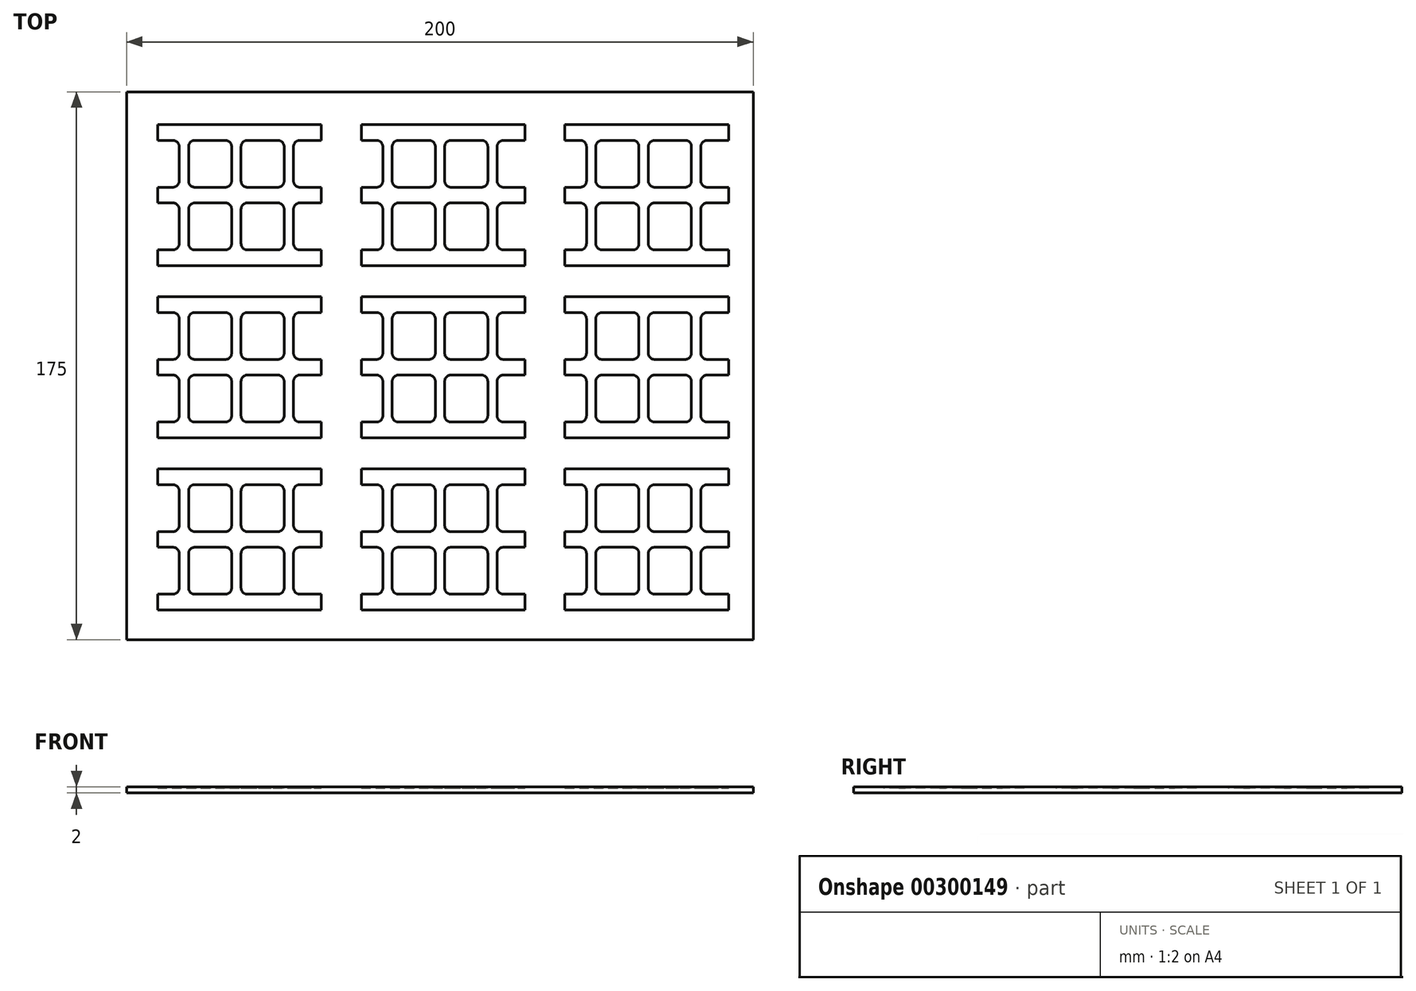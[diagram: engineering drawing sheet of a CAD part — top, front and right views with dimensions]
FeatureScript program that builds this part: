
annotation { "Feature Type Name" : "Feature", "Feature Type Description" : "" }
export const myFeature = defineFeature(function(context is Context, id is Id, definition is map)
    precondition{}
    {
        {
            var Q0;
            Q0=qCreatedBy(makeId("Top.planeOp"),FACE);
            var sketch = newSketch(context, id + "F0", { "sketchPlane" : qUnion([Q0])});
            skLineSegment(sketch, "E0.bottom", {"start": v(-3.5, 2.5) * mm, "end": v(-13.25, 2.5) * mm});
            skLineSegment(sketch, "E0.top", {"start": v(-3.5, 17.5) * mm, "end": v(-13.25, 17.5) * mm});
            skLineSegment(sketch, "E0.left", {"start": v(-1.5, 4.5) * mm, "end": v(-1.5, 15.5) * mm});
            skLineSegment(sketch, "E0.right", {"start": v(-15.25, 4.5) * mm, "end": v(-15.25, 15.5) * mm});
            skPoint(sketch, "E1.visualSharp", {"position": v(-15.25, 17.5) * mm});
            skArc(sketch, "E1.filletArc", {"start": v(-13.25, 17.5) * mm, "mid": v(-14.66, 16.91) * mm, "end": v(-15.25, 15.5) * mm});
            skPoint(sketch, "E2.visualSharp", {"position": v(-1.5, 17.5) * mm});
            skArc(sketch, "E2.filletArc", {"start": v(-1.5, 15.5) * mm, "mid": v(-2.09, 16.91) * mm, "end": v(-3.5, 17.5) * mm});
            skPoint(sketch, "E3.visualSharp", {"position": v(-1.5, 2.5) * mm});
            skArc(sketch, "E3.filletArc", {"start": v(-3.5, 2.5) * mm, "mid": v(-2.09, 3.09) * mm, "end": v(-1.5, 4.5) * mm});
            skPoint(sketch, "E4.visualSharp", {"position": v(-15.25, 2.5) * mm});
            skArc(sketch, "E4.filletArc", {"start": v(-15.25, 4.5) * mm, "mid": v(-14.66, 3.09) * mm, "end": v(-13.25, 2.5) * mm});
            skArc(sketch, "E5.MirrorCS", {"start": v(15.25, 4.5) * mm, "mid": v(14.66, 3.09) * mm, "end": v(13.25, 2.5) * mm});
            skArc(sketch, "E6.MirrorCS", {"start": v(13.25, 17.5) * mm, "mid": v(14.66, 16.91) * mm, "end": v(15.25, 15.5) * mm});
            skArc(sketch, "E7.MirrorCS", {"start": v(3.5, 2.5) * mm, "mid": v(2.09, 3.09) * mm, "end": v(1.5, 4.5) * mm});
            skArc(sketch, "E8.MirrorCS", {"start": v(1.5, 15.5) * mm, "mid": v(2.09, 16.91) * mm, "end": v(3.5, 17.5) * mm});
            skLineSegment(sketch, "E9.MirrorCS", {"start": v(3.5, 17.5) * mm, "end": v(13.25, 17.5) * mm});
            skLineSegment(sketch, "E10.MirrorCS", {"start": v(1.5, 4.5) * mm, "end": v(1.5, 15.5) * mm});
            skPoint(sketch, "E11.MirrorP", {"position": v(1.5, 17.5) * mm});
            skPoint(sketch, "E12.MirrorP", {"position": v(15.25, 2.5) * mm});
            skPoint(sketch, "E13.MirrorP", {"position": v(15.25, 17.5) * mm});
            skPoint(sketch, "E14.MirrorP", {"position": v(1.5, 2.5) * mm});
            skLineSegment(sketch, "E15.MirrorCS", {"start": v(3.5, 2.5) * mm, "end": v(13.25, 2.5) * mm});
            skLineSegment(sketch, "E16.MirrorCS", {"start": v(15.25, 4.5) * mm, "end": v(15.25, 15.5) * mm});
            skArc(sketch, "E17.MirrorCS", {"start": v(-1.5, -15.5) * mm, "mid": v(-2.09, -16.91) * mm, "end": v(-3.5, -17.5) * mm});
            skArc(sketch, "E18.MirrorCS", {"start": v(-3.5, -2.5) * mm, "mid": v(-2.09, -3.09) * mm, "end": v(-1.5, -4.5) * mm});
            skArc(sketch, "E19.MirrorCS", {"start": v(-13.25, -17.5) * mm, "mid": v(-14.66, -16.91) * mm, "end": v(-15.25, -15.5) * mm});
            skArc(sketch, "E20.MirrorCS", {"start": v(15.25, -4.5) * mm, "mid": v(14.66, -3.09) * mm, "end": v(13.25, -2.5) * mm});
            skArc(sketch, "E21.MirrorCS", {"start": v(-15.25, -4.5) * mm, "mid": v(-14.66, -3.09) * mm, "end": v(-13.25, -2.5) * mm});
            skArc(sketch, "E22.MirrorCS", {"start": v(13.25, -17.5) * mm, "mid": v(14.66, -16.91) * mm, "end": v(15.25, -15.5) * mm});
            skArc(sketch, "E23.MirrorCS", {"start": v(3.5, -2.5) * mm, "mid": v(2.09, -3.09) * mm, "end": v(1.5, -4.5) * mm});
            skArc(sketch, "E24.MirrorCS", {"start": v(1.5, -15.5) * mm, "mid": v(2.09, -16.91) * mm, "end": v(3.5, -17.5) * mm});
            skPoint(sketch, "E25.MirrorP", {"position": v(-15.25, -2.5) * mm});
            skLineSegment(sketch, "E26.MirrorCS", {"start": v(-1.5, -4.5) * mm, "end": v(-1.5, -15.5) * mm});
            skLineSegment(sketch, "E27.MirrorCS", {"start": v(15.25, -4.5) * mm, "end": v(15.25, -15.5) * mm});
            skPoint(sketch, "E28.MirrorP", {"position": v(-15.25, -17.5) * mm});
            skLineSegment(sketch, "E29.MirrorCS", {"start": v(3.5, -17.5) * mm, "end": v(13.25, -17.5) * mm});
            skLineSegment(sketch, "E30.MirrorCS", {"start": v(-15.25, -4.5) * mm, "end": v(-15.25, -15.5) * mm});
            skLineSegment(sketch, "E31.MirrorCS", {"start": v(-3.5, -17.5) * mm, "end": v(-13.25, -17.5) * mm});
            skPoint(sketch, "E32.MirrorP", {"position": v(-1.5, -17.5) * mm});
            skLineSegment(sketch, "E33.MirrorCS", {"start": v(1.5, -4.5) * mm, "end": v(1.5, -15.5) * mm});
            skLineSegment(sketch, "E34.MirrorCS", {"start": v(-3.5, -2.5) * mm, "end": v(-13.25, -2.5) * mm});
            skPoint(sketch, "E35.MirrorP", {"position": v(1.5, -17.5) * mm});
            skPoint(sketch, "E36.MirrorP", {"position": v(-1.5, -2.5) * mm});
            skPoint(sketch, "E37.MirrorP", {"position": v(15.25, -2.5) * mm});
            skPoint(sketch, "E38.MirrorP", {"position": v(15.25, -17.5) * mm});
            skPoint(sketch, "E39.MirrorP", {"position": v(1.5, -2.5) * mm});
            skLineSegment(sketch, "E40.MirrorCS", {"start": v(3.5, -2.5) * mm, "end": v(13.25, -2.5) * mm});
            skLineSegment(sketch, "E41", {"start": v(16.75, 36.36) * mm, "end": v(16.75, -33.16) * mm, "construction": true});
            skArc(sketch, "E42.MirrorCS", {"start": v(18.25, 4.5) * mm, "mid": v(18.84, 3.09) * mm, "end": v(20.25, 2.5) * mm});
            skArc(sketch, "E43.MirrorCS", {"start": v(20.25, -17.5) * mm, "mid": v(18.84, -16.91) * mm, "end": v(18.25, -15.5) * mm});
            skArc(sketch, "E44.MirrorCS", {"start": v(20.25, 17.5) * mm, "mid": v(18.84, 16.91) * mm, "end": v(18.25, 15.5) * mm});
            skArc(sketch, "E45.MirrorCS", {"start": v(18.25, -4.5) * mm, "mid": v(18.84, -3.09) * mm, "end": v(20.25, -2.5) * mm});
            skLineSegment(sketch, "E46.MirrorCS", {"start": v(25.12, -2.5) * mm, "end": v(20.25, -2.5) * mm});
            skLineSegment(sketch, "E47.MirrorCS", {"start": v(18.25, -4.5) * mm, "end": v(18.25, -15.5) * mm});
            skPoint(sketch, "E48.MirrorP", {"position": v(18.25, 2.5) * mm});
            skPoint(sketch, "E49.MirrorP", {"position": v(18.25, -2.5) * mm});
            skLineSegment(sketch, "E50.MirrorCS", {"start": v(25.12, 17.5) * mm, "end": v(20.25, 17.5) * mm});
            skPoint(sketch, "E51.MirrorP", {"position": v(18.25, -17.5) * mm});
            skLineSegment(sketch, "E52.MirrorCS", {"start": v(25.12, -17.5) * mm, "end": v(20.25, -17.5) * mm});
            skLineSegment(sketch, "E53.MirrorCS", {"start": v(18.25, 4.5) * mm, "end": v(18.25, 15.5) * mm});
            skPoint(sketch, "E54.MirrorP", {"position": v(18.25, 17.5) * mm});
            skLineSegment(sketch, "E55.MirrorCS", {"start": v(25.12, 2.5) * mm, "end": v(20.25, 2.5) * mm});
            skLineSegment(sketch, "E56.bottom", {"start": v(25.12, 22.5) * mm, "end": v(-25.12, 22.5) * mm});
            skLineSegment(sketch, "E56.top", {"start": v(25.12, -22.5) * mm, "end": v(-25.12, -22.5) * mm});
            skLineSegment(sketch, "E56.left", {"start": v(25.12, 22.5) * mm, "end": v(25.12, 17.5) * mm});
            skLineSegment(sketch, "E56.right", {"start": v(-25.12, 22.5) * mm, "end": v(-25.12, 17.5) * mm});
            skPoint(sketch, "E56.middle", {"position": v(0, 0) * mm});
            skArc(sketch, "E57.MirrorCS", {"start": v(-18.25, 4.5) * mm, "mid": v(-18.84, 3.09) * mm, "end": v(-20.25, 2.5) * mm});
            skArc(sketch, "E58.MirrorCS", {"start": v(-18.25, -4.5) * mm, "mid": v(-18.84, -3.09) * mm, "end": v(-20.25, -2.5) * mm});
            skArc(sketch, "E59.MirrorCS", {"start": v(-20.25, 17.5) * mm, "mid": v(-18.84, 16.91) * mm, "end": v(-18.25, 15.5) * mm});
            skArc(sketch, "E60.MirrorCS", {"start": v(-20.25, -17.5) * mm, "mid": v(-18.84, -16.91) * mm, "end": v(-18.25, -15.5) * mm});
            skPoint(sketch, "E61.MirrorP", {"position": v(-18.25, -2.5) * mm});
            skLineSegment(sketch, "E62.MirrorCS", {"start": v(-18.25, -4.5) * mm, "end": v(-18.25, -15.5) * mm});
            skPoint(sketch, "E63.MirrorP", {"position": v(-32, -17.5) * mm});
            skLineSegment(sketch, "E64.MirrorCS", {"start": v(-25.12, -2.5) * mm, "end": v(-20.25, -2.5) * mm});
            skPoint(sketch, "E65.MirrorP", {"position": v(-18.25, 2.5) * mm});
            skPoint(sketch, "E66.MirrorP", {"position": v(-18.25, 17.5) * mm});
            skPoint(sketch, "E67.MirrorP", {"position": v(-32, 17.5) * mm});
            skPoint(sketch, "E68.MirrorP", {"position": v(-18.25, -17.5) * mm});
            skLineSegment(sketch, "E69.MirrorCS", {"start": v(-25.12, 2.5) * mm, "end": v(-20.25, 2.5) * mm});
            skPoint(sketch, "E70.MirrorP", {"position": v(-32, 2.5) * mm});
            skPoint(sketch, "E71.MirrorP", {"position": v(-32, -2.5) * mm});
            skLineSegment(sketch, "E72.MirrorCS", {"start": v(-25.12, -17.5) * mm, "end": v(-20.25, -17.5) * mm});
            skLineSegment(sketch, "E73.MirrorCS", {"start": v(-25.12, 17.5) * mm, "end": v(-20.25, 17.5) * mm});
            skLineSegment(sketch, "E74.MirrorCS", {"start": v(-18.25, 4.5) * mm, "end": v(-18.25, 15.5) * mm});
            skLineSegment(sketch, "E75.trimOffspring", {"start": v(25.12, 2.5) * mm, "end": v(25.12, -2.5) * mm});
            skLineSegment(sketch, "E76.trimOffspring", {"start": v(25.12, -17.5) * mm, "end": v(25.12, -22.5) * mm});
            skPoint(sketch, "E77.MirrorCS.start.orphan", {"position": v(30, -2.5) * mm});
            skPoint(sketch, "E78.orphan", {"position": v(30, -17.5) * mm});
            skPoint(sketch, "E79.MirrorCS.start.orphan", {"position": v(30, 2.5) * mm});
            skPoint(sketch, "E80.MirrorCS.end.orphan", {"position": v(30, 17.5) * mm});
            skPoint(sketch, "E81.MirrorCS.start.orphan", {"position": v(-32, 15.5) * mm});
            skPoint(sketch, "E82.orphan", {"position": v(-30, 17.5) * mm});
            skLineSegment(sketch, "E83.trimOffspring", {"start": v(-25.12, 2.5) * mm, "end": v(-25.12, -2.5) * mm});
            skPoint(sketch, "E84.MirrorCS.end.orphan", {"position": v(-32, 4.5) * mm});
            skPoint(sketch, "E84.MirrorCS.start.orphan", {"position": v(-30, 2.5) * mm});
            skPoint(sketch, "E85.orphan", {"position": v(-30, -2.5) * mm});
            skPoint(sketch, "E86.MirrorCS.start.orphan", {"position": v(-32, -4.5) * mm});
            skPoint(sketch, "E87.MirrorCS.start.orphan", {"position": v(-32, -15.5) * mm});
            skPoint(sketch, "E88.orphan", {"position": v(-30, -17.5) * mm});
            skLineSegment(sketch, "E89.trimOffspring", {"start": v(-25.12, -17.5) * mm, "end": v(-25.12, -22.5) * mm});
            skLineSegment(sketch, "E90.direction1", {"start": v(-30, -17.5) * mm, "end": v(40, -17.5) * mm, "construction": true});
            skLineSegment(sketch, "E91.bottom", {"start": v(25.12, 22.5) * mm, "end": v(27.12, 22.5) * mm});
            skLineSegment(sketch, "E91.top", {"start": v(25.12, 17.5) * mm, "end": v(27.12, 17.5) * mm});
            skLineSegment(sketch, "E91.right", {"start": v(27.12, 22.5) * mm, "end": v(27.12, 17.5) * mm});
            skLineSegment(sketch, "E92.bottom", {"start": v(25.12, 2.5) * mm, "end": v(27.12, 2.5) * mm});
            skLineSegment(sketch, "E92.top", {"start": v(25.12, -2.5) * mm, "end": v(27.12, -2.5) * mm});
            skLineSegment(sketch, "E92.right", {"start": v(27.12, 2.5) * mm, "end": v(27.12, -2.5) * mm});
            skLineSegment(sketch, "E93.bottom", {"start": v(25.12, -17.5) * mm, "end": v(27.12, -17.5) * mm});
            skLineSegment(sketch, "E93.top", {"start": v(25.12, -22.5) * mm, "end": v(27.12, -22.5) * mm});
            skLineSegment(sketch, "E93.right", {"start": v(27.12, -17.5) * mm, "end": v(27.12, -22.5) * mm});
            skPoint(sketch, "E94.0.1.0", {"position": v(-15.25, 37.5) * mm});
            skPoint(sketch, "E94.0.1.1", {"position": v(-32, 70.5) * mm});
            skLineSegment(sketch, "E94.0.1.2", {"start": v(25.12, 57.5) * mm, "end": v(20.25, 57.5) * mm});
            skLineSegment(sketch, "E94.0.1.3", {"start": v(-18.25, 50.5) * mm, "end": v(-18.25, 39.5) * mm});
            skPoint(sketch, "E94.0.1.4", {"position": v(-15.25, 72.5) * mm});
            skPoint(sketch, "E94.0.1.5", {"position": v(-30, 37.5) * mm});
            skPoint(sketch, "E94.0.1.6", {"position": v(-18.25, 72.5) * mm});
            skPoint(sketch, "E94.0.1.7", {"position": v(-1.5, 37.5) * mm});
            skPoint(sketch, "E94.0.1.8", {"position": v(-32, 57.5) * mm});
            skPoint(sketch, "E94.0.1.9", {"position": v(-30, 72.5) * mm});
            skLineSegment(sketch, "E94.0.1.10", {"start": v(25.12, 77.5) * mm, "end": v(-25.12, 77.5) * mm});
            skLineSegment(sketch, "E94.0.1.11", {"start": v(-15.25, 50.5) * mm, "end": v(-15.25, 39.5) * mm});
            skLineSegment(sketch, "E94.0.1.12", {"start": v(25.12, 37.5) * mm, "end": v(25.12, 32.5) * mm});
            skLineSegment(sketch, "E94.0.1.13", {"start": v(27.12, 77.5) * mm, "end": v(27.12, 72.5) * mm});
            skLineSegment(sketch, "E94.0.1.14", {"start": v(25.12, 77.5) * mm, "end": v(25.12, 72.5) * mm});
            skLineSegment(sketch, "E94.0.1.15", {"start": v(-25.12, 52.5) * mm, "end": v(-20.25, 52.5) * mm});
            skLineSegment(sketch, "E94.0.1.16", {"start": v(1.5, 50.5) * mm, "end": v(1.5, 39.5) * mm});
            skPoint(sketch, "E94.0.1.17", {"position": v(-32, 72.5) * mm});
            skPoint(sketch, "E94.0.1.18", {"position": v(18.25, 57.5) * mm});
            skPoint(sketch, "E94.0.1.19", {"position": v(1.5, 37.5) * mm});
            skPoint(sketch, "E94.0.1.20", {"position": v(-1.5, 57.5) * mm});
            skPoint(sketch, "E94.0.1.21", {"position": v(-32, 52.5) * mm});
            skPoint(sketch, "E94.0.1.22", {"position": v(-32, 59.5) * mm});
            skLineSegment(sketch, "E94.0.1.23", {"start": v(25.12, 32.5) * mm, "end": v(-25.12, 32.5) * mm});
            skLineSegment(sketch, "E94.0.1.24", {"start": v(27.12, 37.5) * mm, "end": v(27.12, 32.5) * mm});
            skLineSegment(sketch, "E94.0.1.25", {"start": v(-25.12, 57.5) * mm, "end": v(-25.12, 52.5) * mm});
            skLineSegment(sketch, "E94.0.1.26", {"start": v(-25.12, 77.5) * mm, "end": v(-25.12, 72.5) * mm});
            skLineSegment(sketch, "E94.0.1.27", {"start": v(25.12, 52.5) * mm, "end": v(20.25, 52.5) * mm});
            skLineSegment(sketch, "E94.0.1.28", {"start": v(-3.5, 52.5) * mm, "end": v(-13.25, 52.5) * mm});
            skPoint(sketch, "E94.0.1.29", {"position": v(-1.5, 72.5) * mm});
            skPoint(sketch, "E94.0.1.30", {"position": v(-18.25, 37.5) * mm});
            skPoint(sketch, "E94.0.1.31", {"position": v(18.25, 52.5) * mm});
            skPoint(sketch, "E94.0.1.32", {"position": v(-1.5, 52.5) * mm});
            skPoint(sketch, "E94.0.1.33", {"position": v(1.5, 72.5) * mm});
            skPoint(sketch, "E94.0.1.34", {"position": v(30, 52.5) * mm});
            skPoint(sketch, "E94.0.1.35", {"position": v(-30, 57.5) * mm});
            skLineSegment(sketch, "E94.0.1.36", {"start": v(-25.12, 37.5) * mm, "end": v(-25.12, 32.5) * mm});
            skLineSegment(sketch, "E94.0.1.37", {"start": v(-25.12, 57.5) * mm, "end": v(-20.25, 57.5) * mm});
            skLineSegment(sketch, "E94.0.1.38", {"start": v(3.5, 52.5) * mm, "end": v(13.25, 52.5) * mm});
            skLineSegment(sketch, "E94.0.1.39", {"start": v(18.25, 50.5) * mm, "end": v(18.25, 39.5) * mm});
            skLineSegment(sketch, "E94.0.1.40", {"start": v(1.5, 59.5) * mm, "end": v(1.5, 70.5) * mm});
            skLineSegment(sketch, "E94.0.1.41", {"start": v(3.5, 57.5) * mm, "end": v(13.25, 57.5) * mm});
            skLineSegment(sketch, "E94.0.1.42", {"start": v(15.25, 59.5) * mm, "end": v(15.25, 70.5) * mm});
            skLineSegment(sketch, "E94.0.1.43", {"start": v(-3.5, 57.5) * mm, "end": v(-13.25, 57.5) * mm});
            skLineSegment(sketch, "E94.0.1.44", {"start": v(-3.5, 72.5) * mm, "end": v(-13.25, 72.5) * mm});
            skLineSegment(sketch, "E94.0.1.45", {"start": v(-1.5, 59.5) * mm, "end": v(-1.5, 70.5) * mm});
            skLineSegment(sketch, "E94.0.1.46", {"start": v(-15.25, 59.5) * mm, "end": v(-15.25, 70.5) * mm});
            skLineSegment(sketch, "E94.0.1.47", {"start": v(3.5, 72.5) * mm, "end": v(13.25, 72.5) * mm});
            skPoint(sketch, "E94.0.1.48", {"position": v(15.25, 57.5) * mm});
            skPoint(sketch, "E94.0.1.49", {"position": v(-30, 52.5) * mm});
            skPoint(sketch, "E94.0.1.50", {"position": v(-18.25, 52.5) * mm});
            skPoint(sketch, "E94.0.1.51", {"position": v(15.25, 52.5) * mm});
            skLineSegment(sketch, "E94.0.1.52", {"start": v(25.12, 72.5) * mm, "end": v(20.25, 72.5) * mm});
            skLineSegment(sketch, "E94.0.1.53", {"start": v(25.12, 57.5) * mm, "end": v(25.12, 52.5) * mm});
            skPoint(sketch, "E94.0.1.54", {"position": v(18.25, 37.5) * mm});
            skPoint(sketch, "E94.0.1.55", {"position": v(-15.25, 57.5) * mm});
            skPoint(sketch, "E94.0.1.56", {"position": v(30, 37.5) * mm});
            skLineSegment(sketch, "E94.0.1.57", {"start": v(-30, 37.5) * mm, "end": v(40, 37.5) * mm, "construction": true});
            skPoint(sketch, "E94.0.1.58", {"position": v(-32, 50.5) * mm});
            skPoint(sketch, "E94.0.1.59", {"position": v(-32, 37.5) * mm});
            skPoint(sketch, "E94.0.1.60", {"position": v(15.25, 37.5) * mm});
            skLineSegment(sketch, "E94.0.1.61", {"start": v(-25.12, 72.5) * mm, "end": v(-20.25, 72.5) * mm});
            skLineSegment(sketch, "E94.0.1.62", {"start": v(-1.5, 50.5) * mm, "end": v(-1.5, 39.5) * mm});
            skLineSegment(sketch, "E94.0.1.63", {"start": v(27.12, 57.5) * mm, "end": v(27.12, 52.5) * mm});
            skPoint(sketch, "E94.0.1.64", {"position": v(18.25, 72.5) * mm});
            skPoint(sketch, "E94.0.1.65", {"position": v(30, 57.5) * mm});
            skPoint(sketch, "E94.0.1.66", {"position": v(15.25, 72.5) * mm});
            skPoint(sketch, "E94.0.1.67", {"position": v(0, 55) * mm});
            skPoint(sketch, "E94.0.1.68", {"position": v(-15.25, 52.5) * mm});
            skLineSegment(sketch, "E94.0.1.69", {"start": v(-18.25, 59.5) * mm, "end": v(-18.25, 70.5) * mm});
            skLineSegment(sketch, "E94.0.1.70", {"start": v(15.25, 50.5) * mm, "end": v(15.25, 39.5) * mm});
            skLineSegment(sketch, "E94.0.1.71", {"start": v(18.25, 59.5) * mm, "end": v(18.25, 70.5) * mm});
            skPoint(sketch, "E94.0.1.72", {"position": v(30, 72.5) * mm});
            skPoint(sketch, "E94.0.1.73", {"position": v(1.5, 57.5) * mm});
            skPoint(sketch, "E94.0.1.74", {"position": v(-32, 39.5) * mm});
            skPoint(sketch, "E94.0.1.75", {"position": v(-18.25, 57.5) * mm});
            skPoint(sketch, "E94.0.1.76", {"position": v(1.5, 52.5) * mm});
            skLineSegment(sketch, "E94.0.1.77", {"start": v(25.12, 57.5) * mm, "end": v(25.12, 52.5) * mm});
            skLineSegment(sketch, "E94.0.1.78", {"start": v(3.5, 37.5) * mm, "end": v(13.25, 37.5) * mm});
            skLineSegment(sketch, "E94.0.1.79", {"start": v(25.12, 77.5) * mm, "end": v(25.12, 72.5) * mm});
            skLineSegment(sketch, "E94.0.1.80", {"start": v(25.12, 37.5) * mm, "end": v(25.12, 32.5) * mm});
            skLineSegment(sketch, "E94.0.1.81", {"start": v(-25.12, 37.5) * mm, "end": v(-25.12, 32.5) * mm});
            skLineSegment(sketch, "E94.0.1.82", {"start": v(-25.12, 57.5) * mm, "end": v(-25.12, 52.5) * mm});
            skLineSegment(sketch, "E94.0.1.83", {"start": v(-3.5, 37.5) * mm, "end": v(-13.25, 37.5) * mm});
            skLineSegment(sketch, "E94.0.1.84", {"start": v(-25.12, 77.5) * mm, "end": v(-25.12, 72.5) * mm});
            skLineSegment(sketch, "E94.0.1.85", {"start": v(-25.12, 37.5) * mm, "end": v(-20.25, 37.5) * mm});
            skLineSegment(sketch, "E94.0.1.86", {"start": v(25.12, 37.5) * mm, "end": v(20.25, 37.5) * mm});
            skLineSegment(sketch, "E94.0.1.87", {"start": v(25.12, 32.5) * mm, "end": v(27.12, 32.5) * mm});
            skArc(sketch, "E94.0.1.88", {"start": v(15.25, 50.5) * mm, "mid": v(14.66, 51.91) * mm, "end": v(13.25, 52.5) * mm});
            skArc(sketch, "E94.0.1.89", {"start": v(20.25, 72.5) * mm, "mid": v(18.84, 71.91) * mm, "end": v(18.25, 70.5) * mm});
            skArc(sketch, "E94.0.1.90", {"start": v(-15.25, 50.5) * mm, "mid": v(-14.66, 51.91) * mm, "end": v(-13.25, 52.5) * mm});
            skArc(sketch, "E94.0.1.91", {"start": v(18.25, 50.5) * mm, "mid": v(18.84, 51.91) * mm, "end": v(20.25, 52.5) * mm});
            skArc(sketch, "E94.0.1.92", {"start": v(13.25, 37.5) * mm, "mid": v(14.66, 38.09) * mm, "end": v(15.25, 39.5) * mm});
            skLineSegment(sketch, "E94.0.1.93", {"start": v(25.12, 57.5) * mm, "end": v(27.12, 57.5) * mm});
            skArc(sketch, "E94.0.1.94", {"start": v(3.5, 52.5) * mm, "mid": v(2.09, 51.91) * mm, "end": v(1.5, 50.5) * mm});
            skLineSegment(sketch, "E94.0.1.95", {"start": v(25.12, 52.5) * mm, "end": v(27.12, 52.5) * mm});
            skArc(sketch, "E94.0.1.96", {"start": v(-18.25, 59.5) * mm, "mid": v(-18.84, 58.09) * mm, "end": v(-20.25, 57.5) * mm});
            skArc(sketch, "E94.0.1.97", {"start": v(-13.25, 72.5) * mm, "mid": v(-14.66, 71.91) * mm, "end": v(-15.25, 70.5) * mm});
            skArc(sketch, "E94.0.1.98", {"start": v(-1.5, 70.5) * mm, "mid": v(-2.09, 71.91) * mm, "end": v(-3.5, 72.5) * mm});
            skArc(sketch, "E94.0.1.99", {"start": v(-3.5, 57.5) * mm, "mid": v(-2.09, 58.09) * mm, "end": v(-1.5, 59.5) * mm});
            skArc(sketch, "E94.0.1.100", {"start": v(-15.25, 59.5) * mm, "mid": v(-14.66, 58.09) * mm, "end": v(-13.25, 57.5) * mm});
            skArc(sketch, "E94.0.1.101", {"start": v(15.25, 59.5) * mm, "mid": v(14.66, 58.09) * mm, "end": v(13.25, 57.5) * mm});
            skArc(sketch, "E94.0.1.102", {"start": v(13.25, 72.5) * mm, "mid": v(14.66, 71.91) * mm, "end": v(15.25, 70.5) * mm});
            skArc(sketch, "E94.0.1.103", {"start": v(3.5, 57.5) * mm, "mid": v(2.09, 58.09) * mm, "end": v(1.5, 59.5) * mm});
            skArc(sketch, "E94.0.1.104", {"start": v(1.5, 70.5) * mm, "mid": v(2.09, 71.91) * mm, "end": v(3.5, 72.5) * mm});
            skArc(sketch, "E94.0.1.105", {"start": v(1.5, 39.5) * mm, "mid": v(2.09, 38.09) * mm, "end": v(3.5, 37.5) * mm});
            skArc(sketch, "E94.0.1.106", {"start": v(-1.5, 39.5) * mm, "mid": v(-2.09, 38.09) * mm, "end": v(-3.5, 37.5) * mm});
            skArc(sketch, "E94.0.1.107", {"start": v(-18.25, 50.5) * mm, "mid": v(-18.84, 51.91) * mm, "end": v(-20.25, 52.5) * mm});
            skArc(sketch, "E94.0.1.108", {"start": v(-3.5, 52.5) * mm, "mid": v(-2.09, 51.91) * mm, "end": v(-1.5, 50.5) * mm});
            skLineSegment(sketch, "E94.0.1.109", {"start": v(25.12, 77.5) * mm, "end": v(27.12, 77.5) * mm});
            skArc(sketch, "E94.0.1.110", {"start": v(-20.25, 72.5) * mm, "mid": v(-18.84, 71.91) * mm, "end": v(-18.25, 70.5) * mm});
            skArc(sketch, "E94.0.1.111", {"start": v(18.25, 59.5) * mm, "mid": v(18.84, 58.09) * mm, "end": v(20.25, 57.5) * mm});
            skLineSegment(sketch, "E94.0.1.112", {"start": v(25.12, 37.5) * mm, "end": v(27.12, 37.5) * mm});
            skArc(sketch, "E94.0.1.113", {"start": v(-13.25, 37.5) * mm, "mid": v(-14.66, 38.09) * mm, "end": v(-15.25, 39.5) * mm});
            skLineSegment(sketch, "E94.0.1.114", {"start": v(25.12, 72.5) * mm, "end": v(27.12, 72.5) * mm});
            skArc(sketch, "E94.0.1.115", {"start": v(-20.25, 37.5) * mm, "mid": v(-18.84, 38.09) * mm, "end": v(-18.25, 39.5) * mm});
            skArc(sketch, "E94.0.1.116", {"start": v(20.25, 37.5) * mm, "mid": v(18.84, 38.09) * mm, "end": v(18.25, 39.5) * mm});
            skPoint(sketch, "E94.0.2.0", {"position": v(-15.25, 92.5) * mm});
            skPoint(sketch, "E94.0.2.1", {"position": v(-32, 125.5) * mm});
            skLineSegment(sketch, "E94.0.2.2", {"start": v(25.12, 112.5) * mm, "end": v(20.25, 112.5) * mm});
            skLineSegment(sketch, "E94.0.2.3", {"start": v(-18.25, 105.5) * mm, "end": v(-18.25, 94.5) * mm});
            skPoint(sketch, "E94.0.2.4", {"position": v(-15.25, 127.5) * mm});
            skPoint(sketch, "E94.0.2.5", {"position": v(-30, 92.5) * mm});
            skPoint(sketch, "E94.0.2.6", {"position": v(-18.25, 127.5) * mm});
            skPoint(sketch, "E94.0.2.7", {"position": v(-1.5, 92.5) * mm});
            skPoint(sketch, "E94.0.2.8", {"position": v(-32, 112.5) * mm});
            skPoint(sketch, "E94.0.2.9", {"position": v(-30, 127.5) * mm});
            skLineSegment(sketch, "E94.0.2.10", {"start": v(25.12, 132.5) * mm, "end": v(-25.12, 132.5) * mm});
            skLineSegment(sketch, "E94.0.2.11", {"start": v(-15.25, 105.5) * mm, "end": v(-15.25, 94.5) * mm});
            skLineSegment(sketch, "E94.0.2.12", {"start": v(25.12, 92.5) * mm, "end": v(25.12, 87.5) * mm});
            skLineSegment(sketch, "E94.0.2.13", {"start": v(27.12, 132.5) * mm, "end": v(27.12, 127.5) * mm});
            skLineSegment(sketch, "E94.0.2.14", {"start": v(25.12, 132.5) * mm, "end": v(25.12, 127.5) * mm});
            skLineSegment(sketch, "E94.0.2.15", {"start": v(-25.12, 107.5) * mm, "end": v(-20.25, 107.5) * mm});
            skLineSegment(sketch, "E94.0.2.16", {"start": v(1.5, 105.5) * mm, "end": v(1.5, 94.5) * mm});
            skPoint(sketch, "E94.0.2.17", {"position": v(-32, 127.5) * mm});
            skPoint(sketch, "E94.0.2.18", {"position": v(18.25, 112.5) * mm});
            skPoint(sketch, "E94.0.2.19", {"position": v(1.5, 92.5) * mm});
            skPoint(sketch, "E94.0.2.20", {"position": v(-1.5, 112.5) * mm});
            skPoint(sketch, "E94.0.2.21", {"position": v(-32, 107.5) * mm});
            skPoint(sketch, "E94.0.2.22", {"position": v(-32, 114.5) * mm});
            skLineSegment(sketch, "E94.0.2.23", {"start": v(25.12, 87.5) * mm, "end": v(-25.12, 87.5) * mm});
            skLineSegment(sketch, "E94.0.2.24", {"start": v(27.12, 92.5) * mm, "end": v(27.12, 87.5) * mm});
            skLineSegment(sketch, "E94.0.2.25", {"start": v(-25.12, 112.5) * mm, "end": v(-25.12, 107.5) * mm});
            skLineSegment(sketch, "E94.0.2.26", {"start": v(-25.12, 132.5) * mm, "end": v(-25.12, 127.5) * mm});
            skLineSegment(sketch, "E94.0.2.27", {"start": v(25.12, 107.5) * mm, "end": v(20.25, 107.5) * mm});
            skLineSegment(sketch, "E94.0.2.28", {"start": v(-3.5, 107.5) * mm, "end": v(-13.25, 107.5) * mm});
            skPoint(sketch, "E94.0.2.29", {"position": v(-1.5, 127.5) * mm});
            skPoint(sketch, "E94.0.2.30", {"position": v(-18.25, 92.5) * mm});
            skPoint(sketch, "E94.0.2.31", {"position": v(18.25, 107.5) * mm});
            skPoint(sketch, "E94.0.2.32", {"position": v(-1.5, 107.5) * mm});
            skPoint(sketch, "E94.0.2.33", {"position": v(1.5, 127.5) * mm});
            skPoint(sketch, "E94.0.2.34", {"position": v(30, 107.5) * mm});
            skPoint(sketch, "E94.0.2.35", {"position": v(-30, 112.5) * mm});
            skLineSegment(sketch, "E94.0.2.36", {"start": v(-25.12, 92.5) * mm, "end": v(-25.12, 87.5) * mm});
            skLineSegment(sketch, "E94.0.2.37", {"start": v(-25.12, 112.5) * mm, "end": v(-20.25, 112.5) * mm});
            skLineSegment(sketch, "E94.0.2.38", {"start": v(3.5, 107.5) * mm, "end": v(13.25, 107.5) * mm});
            skLineSegment(sketch, "E94.0.2.39", {"start": v(18.25, 105.5) * mm, "end": v(18.25, 94.5) * mm});
            skLineSegment(sketch, "E94.0.2.40", {"start": v(1.5, 114.5) * mm, "end": v(1.5, 125.5) * mm});
            skLineSegment(sketch, "E94.0.2.41", {"start": v(3.5, 112.5) * mm, "end": v(13.25, 112.5) * mm});
            skLineSegment(sketch, "E94.0.2.42", {"start": v(15.25, 114.5) * mm, "end": v(15.25, 125.5) * mm});
            skLineSegment(sketch, "E94.0.2.43", {"start": v(-3.5, 112.5) * mm, "end": v(-13.25, 112.5) * mm});
            skLineSegment(sketch, "E94.0.2.44", {"start": v(-3.5, 127.5) * mm, "end": v(-13.25, 127.5) * mm});
            skLineSegment(sketch, "E94.0.2.45", {"start": v(-1.5, 114.5) * mm, "end": v(-1.5, 125.5) * mm});
            skLineSegment(sketch, "E94.0.2.46", {"start": v(-15.25, 114.5) * mm, "end": v(-15.25, 125.5) * mm});
            skLineSegment(sketch, "E94.0.2.47", {"start": v(3.5, 127.5) * mm, "end": v(13.25, 127.5) * mm});
            skPoint(sketch, "E94.0.2.48", {"position": v(15.25, 112.5) * mm});
            skPoint(sketch, "E94.0.2.49", {"position": v(-30, 107.5) * mm});
            skPoint(sketch, "E94.0.2.50", {"position": v(-18.25, 107.5) * mm});
            skPoint(sketch, "E94.0.2.51", {"position": v(15.25, 107.5) * mm});
            skLineSegment(sketch, "E94.0.2.52", {"start": v(25.12, 127.5) * mm, "end": v(20.25, 127.5) * mm});
            skLineSegment(sketch, "E94.0.2.53", {"start": v(25.12, 112.5) * mm, "end": v(25.12, 107.5) * mm});
            skPoint(sketch, "E94.0.2.54", {"position": v(18.25, 92.5) * mm});
            skPoint(sketch, "E94.0.2.55", {"position": v(-15.25, 112.5) * mm});
            skPoint(sketch, "E94.0.2.56", {"position": v(30, 92.5) * mm});
            skLineSegment(sketch, "E94.0.2.57", {"start": v(-30, 92.5) * mm, "end": v(40, 92.5) * mm, "construction": true});
            skPoint(sketch, "E94.0.2.58", {"position": v(-32, 105.5) * mm});
            skPoint(sketch, "E94.0.2.59", {"position": v(-32, 92.5) * mm});
            skPoint(sketch, "E94.0.2.60", {"position": v(15.25, 92.5) * mm});
            skLineSegment(sketch, "E94.0.2.61", {"start": v(-25.12, 127.5) * mm, "end": v(-20.25, 127.5) * mm});
            skLineSegment(sketch, "E94.0.2.62", {"start": v(-1.5, 105.5) * mm, "end": v(-1.5, 94.5) * mm});
            skLineSegment(sketch, "E94.0.2.63", {"start": v(27.12, 112.5) * mm, "end": v(27.12, 107.5) * mm});
            skPoint(sketch, "E94.0.2.64", {"position": v(18.25, 127.5) * mm});
            skPoint(sketch, "E94.0.2.65", {"position": v(30, 112.5) * mm});
            skPoint(sketch, "E94.0.2.66", {"position": v(15.25, 127.5) * mm});
            skPoint(sketch, "E94.0.2.67", {"position": v(0, 110) * mm});
            skPoint(sketch, "E94.0.2.68", {"position": v(-15.25, 107.5) * mm});
            skLineSegment(sketch, "E94.0.2.69", {"start": v(-18.25, 114.5) * mm, "end": v(-18.25, 125.5) * mm});
            skLineSegment(sketch, "E94.0.2.70", {"start": v(15.25, 105.5) * mm, "end": v(15.25, 94.5) * mm});
            skLineSegment(sketch, "E94.0.2.71", {"start": v(18.25, 114.5) * mm, "end": v(18.25, 125.5) * mm});
            skPoint(sketch, "E94.0.2.72", {"position": v(30, 127.5) * mm});
            skPoint(sketch, "E94.0.2.73", {"position": v(1.5, 112.5) * mm});
            skPoint(sketch, "E94.0.2.74", {"position": v(-32, 94.5) * mm});
            skPoint(sketch, "E94.0.2.75", {"position": v(-18.25, 112.5) * mm});
            skPoint(sketch, "E94.0.2.76", {"position": v(1.5, 107.5) * mm});
            skLineSegment(sketch, "E94.0.2.77", {"start": v(25.12, 112.5) * mm, "end": v(25.12, 107.5) * mm});
            skLineSegment(sketch, "E94.0.2.78", {"start": v(3.5, 92.5) * mm, "end": v(13.25, 92.5) * mm});
            skLineSegment(sketch, "E94.0.2.79", {"start": v(25.12, 132.5) * mm, "end": v(25.12, 127.5) * mm});
            skLineSegment(sketch, "E94.0.2.80", {"start": v(25.12, 92.5) * mm, "end": v(25.12, 87.5) * mm});
            skLineSegment(sketch, "E94.0.2.81", {"start": v(-25.12, 92.5) * mm, "end": v(-25.12, 87.5) * mm});
            skLineSegment(sketch, "E94.0.2.82", {"start": v(-25.12, 112.5) * mm, "end": v(-25.12, 107.5) * mm});
            skLineSegment(sketch, "E94.0.2.83", {"start": v(-3.5, 92.5) * mm, "end": v(-13.25, 92.5) * mm});
            skLineSegment(sketch, "E94.0.2.84", {"start": v(-25.12, 132.5) * mm, "end": v(-25.12, 127.5) * mm});
            skLineSegment(sketch, "E94.0.2.85", {"start": v(-25.12, 92.5) * mm, "end": v(-20.25, 92.5) * mm});
            skLineSegment(sketch, "E94.0.2.86", {"start": v(25.12, 92.5) * mm, "end": v(20.25, 92.5) * mm});
            skLineSegment(sketch, "E94.0.2.87", {"start": v(25.12, 87.5) * mm, "end": v(27.12, 87.5) * mm});
            skArc(sketch, "E94.0.2.88", {"start": v(15.25, 105.5) * mm, "mid": v(14.66, 106.91) * mm, "end": v(13.25, 107.5) * mm});
            skArc(sketch, "E94.0.2.89", {"start": v(20.25, 127.5) * mm, "mid": v(18.84, 126.91) * mm, "end": v(18.25, 125.5) * mm});
            skArc(sketch, "E94.0.2.90", {"start": v(-15.25, 105.5) * mm, "mid": v(-14.66, 106.91) * mm, "end": v(-13.25, 107.5) * mm});
            skArc(sketch, "E94.0.2.91", {"start": v(18.25, 105.5) * mm, "mid": v(18.84, 106.91) * mm, "end": v(20.25, 107.5) * mm});
            skArc(sketch, "E94.0.2.92", {"start": v(13.25, 92.5) * mm, "mid": v(14.66, 93.09) * mm, "end": v(15.25, 94.5) * mm});
            skLineSegment(sketch, "E94.0.2.93", {"start": v(25.12, 112.5) * mm, "end": v(27.12, 112.5) * mm});
            skArc(sketch, "E94.0.2.94", {"start": v(3.5, 107.5) * mm, "mid": v(2.09, 106.91) * mm, "end": v(1.5, 105.5) * mm});
            skLineSegment(sketch, "E94.0.2.95", {"start": v(25.12, 107.5) * mm, "end": v(27.12, 107.5) * mm});
            skArc(sketch, "E94.0.2.96", {"start": v(-18.25, 114.5) * mm, "mid": v(-18.84, 113.09) * mm, "end": v(-20.25, 112.5) * mm});
            skArc(sketch, "E94.0.2.97", {"start": v(-13.25, 127.5) * mm, "mid": v(-14.66, 126.91) * mm, "end": v(-15.25, 125.5) * mm});
            skArc(sketch, "E94.0.2.98", {"start": v(-1.5, 125.5) * mm, "mid": v(-2.09, 126.91) * mm, "end": v(-3.5, 127.5) * mm});
            skArc(sketch, "E94.0.2.99", {"start": v(-3.5, 112.5) * mm, "mid": v(-2.09, 113.09) * mm, "end": v(-1.5, 114.5) * mm});
            skArc(sketch, "E94.0.2.100", {"start": v(-15.25, 114.5) * mm, "mid": v(-14.66, 113.09) * mm, "end": v(-13.25, 112.5) * mm});
            skArc(sketch, "E94.0.2.101", {"start": v(15.25, 114.5) * mm, "mid": v(14.66, 113.09) * mm, "end": v(13.25, 112.5) * mm});
            skArc(sketch, "E94.0.2.102", {"start": v(13.25, 127.5) * mm, "mid": v(14.66, 126.91) * mm, "end": v(15.25, 125.5) * mm});
            skArc(sketch, "E94.0.2.103", {"start": v(3.5, 112.5) * mm, "mid": v(2.09, 113.09) * mm, "end": v(1.5, 114.5) * mm});
            skArc(sketch, "E94.0.2.104", {"start": v(1.5, 125.5) * mm, "mid": v(2.09, 126.91) * mm, "end": v(3.5, 127.5) * mm});
            skArc(sketch, "E94.0.2.105", {"start": v(1.5, 94.5) * mm, "mid": v(2.09, 93.09) * mm, "end": v(3.5, 92.5) * mm});
            skArc(sketch, "E94.0.2.106", {"start": v(-1.5, 94.5) * mm, "mid": v(-2.09, 93.09) * mm, "end": v(-3.5, 92.5) * mm});
            skArc(sketch, "E94.0.2.107", {"start": v(-18.25, 105.5) * mm, "mid": v(-18.84, 106.91) * mm, "end": v(-20.25, 107.5) * mm});
            skArc(sketch, "E94.0.2.108", {"start": v(-3.5, 107.5) * mm, "mid": v(-2.09, 106.91) * mm, "end": v(-1.5, 105.5) * mm});
            skLineSegment(sketch, "E94.0.2.109", {"start": v(25.12, 132.5) * mm, "end": v(27.12, 132.5) * mm});
            skArc(sketch, "E94.0.2.110", {"start": v(-20.25, 127.5) * mm, "mid": v(-18.84, 126.91) * mm, "end": v(-18.25, 125.5) * mm});
            skArc(sketch, "E94.0.2.111", {"start": v(18.25, 114.5) * mm, "mid": v(18.84, 113.09) * mm, "end": v(20.25, 112.5) * mm});
            skLineSegment(sketch, "E94.0.2.112", {"start": v(25.12, 92.5) * mm, "end": v(27.12, 92.5) * mm});
            skArc(sketch, "E94.0.2.113", {"start": v(-13.25, 92.5) * mm, "mid": v(-14.66, 93.09) * mm, "end": v(-15.25, 94.5) * mm});
            skLineSegment(sketch, "E94.0.2.114", {"start": v(25.12, 127.5) * mm, "end": v(27.12, 127.5) * mm});
            skArc(sketch, "E94.0.2.115", {"start": v(-20.25, 92.5) * mm, "mid": v(-18.84, 93.09) * mm, "end": v(-18.25, 94.5) * mm});
            skArc(sketch, "E94.0.2.116", {"start": v(20.25, 92.5) * mm, "mid": v(18.84, 93.09) * mm, "end": v(18.25, 94.5) * mm});
            skPoint(sketch, "E94.1.0.0", {"position": v(49.75, -17.5) * mm});
            skPoint(sketch, "E94.1.0.1", {"position": v(33, 15.5) * mm});
            skLineSegment(sketch, "E94.1.0.2", {"start": v(90.13, 2.5) * mm, "end": v(85.25, 2.5) * mm});
            skLineSegment(sketch, "E94.1.0.3", {"start": v(46.75, -4.5) * mm, "end": v(46.75, -15.5) * mm});
            skPoint(sketch, "E94.1.0.4", {"position": v(49.75, 17.5) * mm});
            skPoint(sketch, "E94.1.0.5", {"position": v(35, -17.5) * mm});
            skPoint(sketch, "E94.1.0.6", {"position": v(46.75, 17.5) * mm});
            skPoint(sketch, "E94.1.0.7", {"position": v(63.5, -17.5) * mm});
            skPoint(sketch, "E94.1.0.8", {"position": v(33, 2.5) * mm});
            skPoint(sketch, "E94.1.0.9", {"position": v(35, 17.5) * mm});
            skLineSegment(sketch, "E94.1.0.10", {"start": v(90.13, 22.5) * mm, "end": v(39.88, 22.5) * mm});
            skLineSegment(sketch, "E94.1.0.11", {"start": v(49.75, -4.5) * mm, "end": v(49.75, -15.5) * mm});
            skLineSegment(sketch, "E94.1.0.12", {"start": v(90.12, -17.5) * mm, "end": v(90.12, -22.5) * mm});
            skLineSegment(sketch, "E94.1.0.13", {"start": v(92.12, 22.5) * mm, "end": v(92.12, 17.5) * mm});
            skLineSegment(sketch, "E94.1.0.14", {"start": v(90.12, 22.5) * mm, "end": v(90.12, 17.5) * mm});
            skLineSegment(sketch, "E94.1.0.15", {"start": v(39.88, -2.5) * mm, "end": v(44.75, -2.5) * mm});
            skLineSegment(sketch, "E94.1.0.16", {"start": v(66.5, -4.5) * mm, "end": v(66.5, -15.5) * mm});
            skPoint(sketch, "E94.1.0.17", {"position": v(33, 17.5) * mm});
            skPoint(sketch, "E94.1.0.18", {"position": v(83.25, 2.5) * mm});
            skPoint(sketch, "E94.1.0.19", {"position": v(66.5, -17.5) * mm});
            skPoint(sketch, "E94.1.0.20", {"position": v(63.5, 2.5) * mm});
            skPoint(sketch, "E94.1.0.21", {"position": v(33, -2.5) * mm});
            skPoint(sketch, "E94.1.0.22", {"position": v(33, 4.5) * mm});
            skLineSegment(sketch, "E94.1.0.23", {"start": v(90.12, -22.5) * mm, "end": v(39.87, -22.5) * mm});
            skLineSegment(sketch, "E94.1.0.24", {"start": v(92.12, -17.5) * mm, "end": v(92.12, -22.5) * mm});
            skLineSegment(sketch, "E94.1.0.25", {"start": v(39.88, 2.5) * mm, "end": v(39.88, -2.5) * mm});
            skLineSegment(sketch, "E94.1.0.26", {"start": v(39.88, 22.5) * mm, "end": v(39.88, 17.5) * mm});
            skLineSegment(sketch, "E94.1.0.27", {"start": v(90.13, -2.5) * mm, "end": v(85.25, -2.5) * mm});
            skLineSegment(sketch, "E94.1.0.28", {"start": v(61.5, -2.5) * mm, "end": v(51.75, -2.5) * mm});
            skPoint(sketch, "E94.1.0.29", {"position": v(63.5, 17.5) * mm});
            skPoint(sketch, "E94.1.0.30", {"position": v(46.75, -17.5) * mm});
            skPoint(sketch, "E94.1.0.31", {"position": v(83.25, -2.5) * mm});
            skPoint(sketch, "E94.1.0.32", {"position": v(63.5, -2.5) * mm});
            skPoint(sketch, "E94.1.0.33", {"position": v(66.5, 17.5) * mm});
            skPoint(sketch, "E94.1.0.34", {"position": v(95, -2.5) * mm});
            skPoint(sketch, "E94.1.0.35", {"position": v(35, 2.5) * mm});
            skLineSegment(sketch, "E94.1.0.36", {"start": v(39.88, -17.5) * mm, "end": v(39.88, -22.5) * mm});
            skLineSegment(sketch, "E94.1.0.37", {"start": v(39.88, 2.5) * mm, "end": v(44.75, 2.5) * mm});
            skLineSegment(sketch, "E94.1.0.38", {"start": v(68.5, -2.5) * mm, "end": v(78.25, -2.5) * mm});
            skLineSegment(sketch, "E94.1.0.39", {"start": v(83.25, -4.5) * mm, "end": v(83.25, -15.5) * mm});
            skLineSegment(sketch, "E94.1.0.40", {"start": v(66.5, 4.5) * mm, "end": v(66.5, 15.5) * mm});
            skLineSegment(sketch, "E94.1.0.41", {"start": v(68.5, 2.5) * mm, "end": v(78.25, 2.5) * mm});
            skLineSegment(sketch, "E94.1.0.42", {"start": v(80.25, 4.5) * mm, "end": v(80.25, 15.5) * mm});
            skLineSegment(sketch, "E94.1.0.43", {"start": v(61.5, 2.5) * mm, "end": v(51.75, 2.5) * mm});
            skLineSegment(sketch, "E94.1.0.44", {"start": v(61.5, 17.5) * mm, "end": v(51.75, 17.5) * mm});
            skLineSegment(sketch, "E94.1.0.45", {"start": v(63.5, 4.5) * mm, "end": v(63.5, 15.5) * mm});
            skLineSegment(sketch, "E94.1.0.46", {"start": v(49.75, 4.5) * mm, "end": v(49.75, 15.5) * mm});
            skLineSegment(sketch, "E94.1.0.47", {"start": v(68.5, 17.5) * mm, "end": v(78.25, 17.5) * mm});
            skPoint(sketch, "E94.1.0.48", {"position": v(80.25, 2.5) * mm});
            skPoint(sketch, "E94.1.0.49", {"position": v(35, -2.5) * mm});
            skPoint(sketch, "E94.1.0.50", {"position": v(46.75, -2.5) * mm});
            skPoint(sketch, "E94.1.0.51", {"position": v(80.25, -2.5) * mm});
            skLineSegment(sketch, "E94.1.0.52", {"start": v(90.12, 17.5) * mm, "end": v(85.25, 17.5) * mm});
            skLineSegment(sketch, "E94.1.0.53", {"start": v(90.12, 2.5) * mm, "end": v(90.12, -2.5) * mm});
            skPoint(sketch, "E94.1.0.54", {"position": v(83.25, -17.5) * mm});
            skPoint(sketch, "E94.1.0.55", {"position": v(49.75, 2.5) * mm});
            skPoint(sketch, "E94.1.0.56", {"position": v(95, -17.5) * mm});
            skLineSegment(sketch, "E94.1.0.57", {"start": v(35, -17.5) * mm, "end": v(105, -17.5) * mm, "construction": true});
            skPoint(sketch, "E94.1.0.58", {"position": v(33, -4.5) * mm});
            skPoint(sketch, "E94.1.0.59", {"position": v(33, -17.5) * mm});
            skPoint(sketch, "E94.1.0.60", {"position": v(80.25, -17.5) * mm});
            skLineSegment(sketch, "E94.1.0.61", {"start": v(39.88, 17.5) * mm, "end": v(44.75, 17.5) * mm});
            skLineSegment(sketch, "E94.1.0.62", {"start": v(63.5, -4.5) * mm, "end": v(63.5, -15.5) * mm});
            skLineSegment(sketch, "E94.1.0.63", {"start": v(92.12, 2.5) * mm, "end": v(92.12, -2.5) * mm});
            skPoint(sketch, "E94.1.0.64", {"position": v(83.25, 17.5) * mm});
            skPoint(sketch, "E94.1.0.65", {"position": v(95, 2.5) * mm});
            skPoint(sketch, "E94.1.0.66", {"position": v(80.25, 17.5) * mm});
            skPoint(sketch, "E94.1.0.67", {"position": v(65, 0) * mm});
            skPoint(sketch, "E94.1.0.68", {"position": v(49.75, -2.5) * mm});
            skLineSegment(sketch, "E94.1.0.69", {"start": v(46.75, 4.5) * mm, "end": v(46.75, 15.5) * mm});
            skLineSegment(sketch, "E94.1.0.70", {"start": v(80.25, -4.5) * mm, "end": v(80.25, -15.5) * mm});
            skLineSegment(sketch, "E94.1.0.71", {"start": v(83.25, 4.5) * mm, "end": v(83.25, 15.5) * mm});
            skPoint(sketch, "E94.1.0.72", {"position": v(95, 17.5) * mm});
            skPoint(sketch, "E94.1.0.73", {"position": v(66.5, 2.5) * mm});
            skPoint(sketch, "E94.1.0.74", {"position": v(33, -15.5) * mm});
            skPoint(sketch, "E94.1.0.75", {"position": v(46.75, 2.5) * mm});
            skPoint(sketch, "E94.1.0.76", {"position": v(66.5, -2.5) * mm});
            skLineSegment(sketch, "E94.1.0.77", {"start": v(90.12, 2.5) * mm, "end": v(90.12, -2.5) * mm});
            skLineSegment(sketch, "E94.1.0.78", {"start": v(68.5, -17.5) * mm, "end": v(78.25, -17.5) * mm});
            skLineSegment(sketch, "E94.1.0.79", {"start": v(90.13, 22.5) * mm, "end": v(90.13, 17.5) * mm});
            skLineSegment(sketch, "E94.1.0.80", {"start": v(90.12, -17.5) * mm, "end": v(90.12, -22.5) * mm});
            skLineSegment(sketch, "E94.1.0.81", {"start": v(39.88, -17.5) * mm, "end": v(39.88, -22.5) * mm});
            skLineSegment(sketch, "E94.1.0.82", {"start": v(39.88, 2.5) * mm, "end": v(39.88, -2.5) * mm});
            skLineSegment(sketch, "E94.1.0.83", {"start": v(61.5, -17.5) * mm, "end": v(51.75, -17.5) * mm});
            skLineSegment(sketch, "E94.1.0.84", {"start": v(39.88, 22.5) * mm, "end": v(39.88, 17.5) * mm});
            skLineSegment(sketch, "E94.1.0.85", {"start": v(39.88, -17.5) * mm, "end": v(44.75, -17.5) * mm});
            skLineSegment(sketch, "E94.1.0.86", {"start": v(90.13, -17.5) * mm, "end": v(85.25, -17.5) * mm});
            skLineSegment(sketch, "E94.1.0.87", {"start": v(90.13, -22.5) * mm, "end": v(92.13, -22.5) * mm});
            skArc(sketch, "E94.1.0.88", {"start": v(80.25, -4.5) * mm, "mid": v(79.66, -3.09) * mm, "end": v(78.25, -2.5) * mm});
            skArc(sketch, "E94.1.0.89", {"start": v(85.25, 17.5) * mm, "mid": v(83.84, 16.91) * mm, "end": v(83.25, 15.5) * mm});
            skArc(sketch, "E94.1.0.90", {"start": v(49.75, -4.5) * mm, "mid": v(50.34, -3.09) * mm, "end": v(51.75, -2.5) * mm});
            skArc(sketch, "E94.1.0.91", {"start": v(83.25, -4.5) * mm, "mid": v(83.84, -3.09) * mm, "end": v(85.25, -2.5) * mm});
            skArc(sketch, "E94.1.0.92", {"start": v(78.25, -17.5) * mm, "mid": v(79.66, -16.91) * mm, "end": v(80.25, -15.5) * mm});
            skLineSegment(sketch, "E94.1.0.93", {"start": v(90.13, 2.5) * mm, "end": v(92.13, 2.5) * mm});
            skArc(sketch, "E94.1.0.94", {"start": v(68.5, -2.5) * mm, "mid": v(67.09, -3.09) * mm, "end": v(66.5, -4.5) * mm});
            skLineSegment(sketch, "E94.1.0.95", {"start": v(90.13, -2.5) * mm, "end": v(92.13, -2.5) * mm});
            skArc(sketch, "E94.1.0.96", {"start": v(46.75, 4.5) * mm, "mid": v(46.16, 3.09) * mm, "end": v(44.75, 2.5) * mm});
            skArc(sketch, "E94.1.0.97", {"start": v(51.75, 17.5) * mm, "mid": v(50.34, 16.91) * mm, "end": v(49.75, 15.5) * mm});
            skArc(sketch, "E94.1.0.98", {"start": v(63.5, 15.5) * mm, "mid": v(62.91, 16.91) * mm, "end": v(61.5, 17.5) * mm});
            skArc(sketch, "E94.1.0.99", {"start": v(61.5, 2.5) * mm, "mid": v(62.91, 3.09) * mm, "end": v(63.5, 4.5) * mm});
            skArc(sketch, "E94.1.0.100", {"start": v(49.75, 4.5) * mm, "mid": v(50.34, 3.09) * mm, "end": v(51.75, 2.5) * mm});
            skArc(sketch, "E94.1.0.101", {"start": v(80.25, 4.5) * mm, "mid": v(79.66, 3.09) * mm, "end": v(78.25, 2.5) * mm});
            skArc(sketch, "E94.1.0.102", {"start": v(78.25, 17.5) * mm, "mid": v(79.66, 16.91) * mm, "end": v(80.25, 15.5) * mm});
            skArc(sketch, "E94.1.0.103", {"start": v(68.5, 2.5) * mm, "mid": v(67.09, 3.09) * mm, "end": v(66.5, 4.5) * mm});
            skArc(sketch, "E94.1.0.104", {"start": v(66.5, 15.5) * mm, "mid": v(67.09, 16.91) * mm, "end": v(68.5, 17.5) * mm});
            skArc(sketch, "E94.1.0.105", {"start": v(66.5, -15.5) * mm, "mid": v(67.09, -16.91) * mm, "end": v(68.5, -17.5) * mm});
            skArc(sketch, "E94.1.0.106", {"start": v(63.5, -15.5) * mm, "mid": v(62.91, -16.91) * mm, "end": v(61.5, -17.5) * mm});
            skArc(sketch, "E94.1.0.107", {"start": v(46.75, -4.5) * mm, "mid": v(46.16, -3.09) * mm, "end": v(44.75, -2.5) * mm});
            skArc(sketch, "E94.1.0.108", {"start": v(61.5, -2.5) * mm, "mid": v(62.91, -3.09) * mm, "end": v(63.5, -4.5) * mm});
            skLineSegment(sketch, "E94.1.0.109", {"start": v(90.13, 22.5) * mm, "end": v(92.12, 22.5) * mm});
            skArc(sketch, "E94.1.0.110", {"start": v(44.75, 17.5) * mm, "mid": v(46.16, 16.91) * mm, "end": v(46.75, 15.5) * mm});
            skArc(sketch, "E94.1.0.111", {"start": v(83.25, 4.5) * mm, "mid": v(83.84, 3.09) * mm, "end": v(85.25, 2.5) * mm});
            skLineSegment(sketch, "E94.1.0.112", {"start": v(90.13, -17.5) * mm, "end": v(92.13, -17.5) * mm});
            skArc(sketch, "E94.1.0.113", {"start": v(51.75, -17.5) * mm, "mid": v(50.34, -16.91) * mm, "end": v(49.75, -15.5) * mm});
            skLineSegment(sketch, "E94.1.0.114", {"start": v(90.13, 17.5) * mm, "end": v(92.12, 17.5) * mm});
            skArc(sketch, "E94.1.0.115", {"start": v(44.75, -17.5) * mm, "mid": v(46.16, -16.91) * mm, "end": v(46.75, -15.5) * mm});
            skArc(sketch, "E94.1.0.116", {"start": v(85.25, -17.5) * mm, "mid": v(83.84, -16.91) * mm, "end": v(83.25, -15.5) * mm});
            skPoint(sketch, "E94.1.1.0", {"position": v(49.75, 37.5) * mm});
            skPoint(sketch, "E94.1.1.1", {"position": v(33, 70.5) * mm});
            skLineSegment(sketch, "E94.1.1.2", {"start": v(90.13, 57.5) * mm, "end": v(85.25, 57.5) * mm});
            skLineSegment(sketch, "E94.1.1.3", {"start": v(46.75, 50.5) * mm, "end": v(46.75, 39.5) * mm});
            skPoint(sketch, "E94.1.1.4", {"position": v(49.75, 72.5) * mm});
            skPoint(sketch, "E94.1.1.5", {"position": v(35, 37.5) * mm});
            skPoint(sketch, "E94.1.1.6", {"position": v(46.75, 72.5) * mm});
            skPoint(sketch, "E94.1.1.7", {"position": v(63.5, 37.5) * mm});
            skPoint(sketch, "E94.1.1.8", {"position": v(33, 57.5) * mm});
            skPoint(sketch, "E94.1.1.9", {"position": v(35, 72.5) * mm});
            skLineSegment(sketch, "E94.1.1.10", {"start": v(90.13, 77.5) * mm, "end": v(39.88, 77.5) * mm});
            skLineSegment(sketch, "E94.1.1.11", {"start": v(49.75, 50.5) * mm, "end": v(49.75, 39.5) * mm});
            skLineSegment(sketch, "E94.1.1.12", {"start": v(90.12, 37.5) * mm, "end": v(90.12, 32.5) * mm});
            skLineSegment(sketch, "E94.1.1.13", {"start": v(92.12, 77.5) * mm, "end": v(92.12, 72.5) * mm});
            skLineSegment(sketch, "E94.1.1.14", {"start": v(90.12, 77.5) * mm, "end": v(90.12, 72.5) * mm});
            skLineSegment(sketch, "E94.1.1.15", {"start": v(39.88, 52.5) * mm, "end": v(44.75, 52.5) * mm});
            skLineSegment(sketch, "E94.1.1.16", {"start": v(66.5, 50.5) * mm, "end": v(66.5, 39.5) * mm});
            skPoint(sketch, "E94.1.1.17", {"position": v(33, 72.5) * mm});
            skPoint(sketch, "E94.1.1.18", {"position": v(83.25, 57.5) * mm});
            skPoint(sketch, "E94.1.1.19", {"position": v(66.5, 37.5) * mm});
            skPoint(sketch, "E94.1.1.20", {"position": v(63.5, 57.5) * mm});
            skPoint(sketch, "E94.1.1.21", {"position": v(33, 52.5) * mm});
            skPoint(sketch, "E94.1.1.22", {"position": v(33, 59.5) * mm});
            skLineSegment(sketch, "E94.1.1.23", {"start": v(90.12, 32.5) * mm, "end": v(39.87, 32.5) * mm});
            skLineSegment(sketch, "E94.1.1.24", {"start": v(92.12, 37.5) * mm, "end": v(92.12, 32.5) * mm});
            skLineSegment(sketch, "E94.1.1.25", {"start": v(39.88, 57.5) * mm, "end": v(39.88, 52.5) * mm});
            skLineSegment(sketch, "E94.1.1.26", {"start": v(39.88, 77.5) * mm, "end": v(39.88, 72.5) * mm});
            skLineSegment(sketch, "E94.1.1.27", {"start": v(90.13, 52.5) * mm, "end": v(85.25, 52.5) * mm});
            skLineSegment(sketch, "E94.1.1.28", {"start": v(61.5, 52.5) * mm, "end": v(51.75, 52.5) * mm});
            skPoint(sketch, "E94.1.1.29", {"position": v(63.5, 72.5) * mm});
            skPoint(sketch, "E94.1.1.30", {"position": v(46.75, 37.5) * mm});
            skPoint(sketch, "E94.1.1.31", {"position": v(83.25, 52.5) * mm});
            skPoint(sketch, "E94.1.1.32", {"position": v(63.5, 52.5) * mm});
            skPoint(sketch, "E94.1.1.33", {"position": v(66.5, 72.5) * mm});
            skPoint(sketch, "E94.1.1.34", {"position": v(95, 52.5) * mm});
            skPoint(sketch, "E94.1.1.35", {"position": v(35, 57.5) * mm});
            skLineSegment(sketch, "E94.1.1.36", {"start": v(39.88, 37.5) * mm, "end": v(39.88, 32.5) * mm});
            skLineSegment(sketch, "E94.1.1.37", {"start": v(39.88, 57.5) * mm, "end": v(44.75, 57.5) * mm});
            skLineSegment(sketch, "E94.1.1.38", {"start": v(68.5, 52.5) * mm, "end": v(78.25, 52.5) * mm});
            skLineSegment(sketch, "E94.1.1.39", {"start": v(83.25, 50.5) * mm, "end": v(83.25, 39.5) * mm});
            skLineSegment(sketch, "E94.1.1.40", {"start": v(66.5, 59.5) * mm, "end": v(66.5, 70.5) * mm});
            skLineSegment(sketch, "E94.1.1.41", {"start": v(68.5, 57.5) * mm, "end": v(78.25, 57.5) * mm});
            skLineSegment(sketch, "E94.1.1.42", {"start": v(80.25, 59.5) * mm, "end": v(80.25, 70.5) * mm});
            skLineSegment(sketch, "E94.1.1.43", {"start": v(61.5, 57.5) * mm, "end": v(51.75, 57.5) * mm});
            skLineSegment(sketch, "E94.1.1.44", {"start": v(61.5, 72.5) * mm, "end": v(51.75, 72.5) * mm});
            skLineSegment(sketch, "E94.1.1.45", {"start": v(63.5, 59.5) * mm, "end": v(63.5, 70.5) * mm});
            skLineSegment(sketch, "E94.1.1.46", {"start": v(49.75, 59.5) * mm, "end": v(49.75, 70.5) * mm});
            skLineSegment(sketch, "E94.1.1.47", {"start": v(68.5, 72.5) * mm, "end": v(78.25, 72.5) * mm});
            skPoint(sketch, "E94.1.1.48", {"position": v(80.25, 57.5) * mm});
            skPoint(sketch, "E94.1.1.49", {"position": v(35, 52.5) * mm});
            skPoint(sketch, "E94.1.1.50", {"position": v(46.75, 52.5) * mm});
            skPoint(sketch, "E94.1.1.51", {"position": v(80.25, 52.5) * mm});
            skLineSegment(sketch, "E94.1.1.52", {"start": v(90.12, 72.5) * mm, "end": v(85.25, 72.5) * mm});
            skLineSegment(sketch, "E94.1.1.53", {"start": v(90.12, 57.5) * mm, "end": v(90.12, 52.5) * mm});
            skPoint(sketch, "E94.1.1.54", {"position": v(83.25, 37.5) * mm});
            skPoint(sketch, "E94.1.1.55", {"position": v(49.75, 57.5) * mm});
            skPoint(sketch, "E94.1.1.56", {"position": v(95, 37.5) * mm});
            skLineSegment(sketch, "E94.1.1.57", {"start": v(35, 37.5) * mm, "end": v(105, 37.5) * mm, "construction": true});
            skPoint(sketch, "E94.1.1.58", {"position": v(33, 50.5) * mm});
            skPoint(sketch, "E94.1.1.59", {"position": v(33, 37.5) * mm});
            skPoint(sketch, "E94.1.1.60", {"position": v(80.25, 37.5) * mm});
            skLineSegment(sketch, "E94.1.1.61", {"start": v(39.88, 72.5) * mm, "end": v(44.75, 72.5) * mm});
            skLineSegment(sketch, "E94.1.1.62", {"start": v(63.5, 50.5) * mm, "end": v(63.5, 39.5) * mm});
            skLineSegment(sketch, "E94.1.1.63", {"start": v(92.12, 57.5) * mm, "end": v(92.12, 52.5) * mm});
            skPoint(sketch, "E94.1.1.64", {"position": v(83.25, 72.5) * mm});
            skPoint(sketch, "E94.1.1.65", {"position": v(95, 57.5) * mm});
            skPoint(sketch, "E94.1.1.66", {"position": v(80.25, 72.5) * mm});
            skPoint(sketch, "E94.1.1.67", {"position": v(65, 55) * mm});
            skPoint(sketch, "E94.1.1.68", {"position": v(49.75, 52.5) * mm});
            skLineSegment(sketch, "E94.1.1.69", {"start": v(46.75, 59.5) * mm, "end": v(46.75, 70.5) * mm});
            skLineSegment(sketch, "E94.1.1.70", {"start": v(80.25, 50.5) * mm, "end": v(80.25, 39.5) * mm});
            skLineSegment(sketch, "E94.1.1.71", {"start": v(83.25, 59.5) * mm, "end": v(83.25, 70.5) * mm});
            skPoint(sketch, "E94.1.1.72", {"position": v(95, 72.5) * mm});
            skPoint(sketch, "E94.1.1.73", {"position": v(66.5, 57.5) * mm});
            skPoint(sketch, "E94.1.1.74", {"position": v(33, 39.5) * mm});
            skPoint(sketch, "E94.1.1.75", {"position": v(46.75, 57.5) * mm});
            skPoint(sketch, "E94.1.1.76", {"position": v(66.5, 52.5) * mm});
            skLineSegment(sketch, "E94.1.1.77", {"start": v(90.12, 57.5) * mm, "end": v(90.12, 52.5) * mm});
            skLineSegment(sketch, "E94.1.1.78", {"start": v(68.5, 37.5) * mm, "end": v(78.25, 37.5) * mm});
            skLineSegment(sketch, "E94.1.1.79", {"start": v(90.13, 77.5) * mm, "end": v(90.13, 72.5) * mm});
            skLineSegment(sketch, "E94.1.1.80", {"start": v(90.12, 37.5) * mm, "end": v(90.12, 32.5) * mm});
            skLineSegment(sketch, "E94.1.1.81", {"start": v(39.88, 37.5) * mm, "end": v(39.88, 32.5) * mm});
            skLineSegment(sketch, "E94.1.1.82", {"start": v(39.88, 57.5) * mm, "end": v(39.88, 52.5) * mm});
            skLineSegment(sketch, "E94.1.1.83", {"start": v(61.5, 37.5) * mm, "end": v(51.75, 37.5) * mm});
            skLineSegment(sketch, "E94.1.1.84", {"start": v(39.88, 77.5) * mm, "end": v(39.88, 72.5) * mm});
            skLineSegment(sketch, "E94.1.1.85", {"start": v(39.88, 37.5) * mm, "end": v(44.75, 37.5) * mm});
            skLineSegment(sketch, "E94.1.1.86", {"start": v(90.13, 37.5) * mm, "end": v(85.25, 37.5) * mm});
            skLineSegment(sketch, "E94.1.1.87", {"start": v(90.13, 32.5) * mm, "end": v(92.13, 32.5) * mm});
            skArc(sketch, "E94.1.1.88", {"start": v(80.25, 50.5) * mm, "mid": v(79.66, 51.91) * mm, "end": v(78.25, 52.5) * mm});
            skArc(sketch, "E94.1.1.89", {"start": v(85.25, 72.5) * mm, "mid": v(83.84, 71.91) * mm, "end": v(83.25, 70.5) * mm});
            skArc(sketch, "E94.1.1.90", {"start": v(49.75, 50.5) * mm, "mid": v(50.34, 51.91) * mm, "end": v(51.75, 52.5) * mm});
            skArc(sketch, "E94.1.1.91", {"start": v(83.25, 50.5) * mm, "mid": v(83.84, 51.91) * mm, "end": v(85.25, 52.5) * mm});
            skArc(sketch, "E94.1.1.92", {"start": v(78.25, 37.5) * mm, "mid": v(79.66, 38.09) * mm, "end": v(80.25, 39.5) * mm});
            skLineSegment(sketch, "E94.1.1.93", {"start": v(90.13, 57.5) * mm, "end": v(92.13, 57.5) * mm});
            skArc(sketch, "E94.1.1.94", {"start": v(68.5, 52.5) * mm, "mid": v(67.09, 51.91) * mm, "end": v(66.5, 50.5) * mm});
            skLineSegment(sketch, "E94.1.1.95", {"start": v(90.13, 52.5) * mm, "end": v(92.13, 52.5) * mm});
            skArc(sketch, "E94.1.1.96", {"start": v(46.75, 59.5) * mm, "mid": v(46.16, 58.09) * mm, "end": v(44.75, 57.5) * mm});
            skArc(sketch, "E94.1.1.97", {"start": v(51.75, 72.5) * mm, "mid": v(50.34, 71.91) * mm, "end": v(49.75, 70.5) * mm});
            skArc(sketch, "E94.1.1.98", {"start": v(63.5, 70.5) * mm, "mid": v(62.91, 71.91) * mm, "end": v(61.5, 72.5) * mm});
            skArc(sketch, "E94.1.1.99", {"start": v(61.5, 57.5) * mm, "mid": v(62.91, 58.09) * mm, "end": v(63.5, 59.5) * mm});
            skArc(sketch, "E94.1.1.100", {"start": v(49.75, 59.5) * mm, "mid": v(50.34, 58.09) * mm, "end": v(51.75, 57.5) * mm});
            skArc(sketch, "E94.1.1.101", {"start": v(80.25, 59.5) * mm, "mid": v(79.66, 58.09) * mm, "end": v(78.25, 57.5) * mm});
            skArc(sketch, "E94.1.1.102", {"start": v(78.25, 72.5) * mm, "mid": v(79.66, 71.91) * mm, "end": v(80.25, 70.5) * mm});
            skArc(sketch, "E94.1.1.103", {"start": v(68.5, 57.5) * mm, "mid": v(67.09, 58.09) * mm, "end": v(66.5, 59.5) * mm});
            skArc(sketch, "E94.1.1.104", {"start": v(66.5, 70.5) * mm, "mid": v(67.09, 71.91) * mm, "end": v(68.5, 72.5) * mm});
            skArc(sketch, "E94.1.1.105", {"start": v(66.5, 39.5) * mm, "mid": v(67.09, 38.09) * mm, "end": v(68.5, 37.5) * mm});
            skArc(sketch, "E94.1.1.106", {"start": v(63.5, 39.5) * mm, "mid": v(62.91, 38.09) * mm, "end": v(61.5, 37.5) * mm});
            skArc(sketch, "E94.1.1.107", {"start": v(46.75, 50.5) * mm, "mid": v(46.16, 51.91) * mm, "end": v(44.75, 52.5) * mm});
            skArc(sketch, "E94.1.1.108", {"start": v(61.5, 52.5) * mm, "mid": v(62.91, 51.91) * mm, "end": v(63.5, 50.5) * mm});
            skLineSegment(sketch, "E94.1.1.109", {"start": v(90.13, 77.5) * mm, "end": v(92.12, 77.5) * mm});
            skArc(sketch, "E94.1.1.110", {"start": v(44.75, 72.5) * mm, "mid": v(46.16, 71.91) * mm, "end": v(46.75, 70.5) * mm});
            skArc(sketch, "E94.1.1.111", {"start": v(83.25, 59.5) * mm, "mid": v(83.84, 58.09) * mm, "end": v(85.25, 57.5) * mm});
            skLineSegment(sketch, "E94.1.1.112", {"start": v(90.13, 37.5) * mm, "end": v(92.13, 37.5) * mm});
            skArc(sketch, "E94.1.1.113", {"start": v(51.75, 37.5) * mm, "mid": v(50.34, 38.09) * mm, "end": v(49.75, 39.5) * mm});
            skLineSegment(sketch, "E94.1.1.114", {"start": v(90.13, 72.5) * mm, "end": v(92.12, 72.5) * mm});
            skArc(sketch, "E94.1.1.115", {"start": v(44.75, 37.5) * mm, "mid": v(46.16, 38.09) * mm, "end": v(46.75, 39.5) * mm});
            skArc(sketch, "E94.1.1.116", {"start": v(85.25, 37.5) * mm, "mid": v(83.84, 38.09) * mm, "end": v(83.25, 39.5) * mm});
            skPoint(sketch, "E94.1.2.0", {"position": v(49.75, 92.5) * mm});
            skPoint(sketch, "E94.1.2.1", {"position": v(33, 125.5) * mm});
            skLineSegment(sketch, "E94.1.2.2", {"start": v(90.13, 112.5) * mm, "end": v(85.25, 112.5) * mm});
            skLineSegment(sketch, "E94.1.2.3", {"start": v(46.75, 105.5) * mm, "end": v(46.75, 94.5) * mm});
            skPoint(sketch, "E94.1.2.4", {"position": v(49.75, 127.5) * mm});
            skPoint(sketch, "E94.1.2.5", {"position": v(35, 92.5) * mm});
            skPoint(sketch, "E94.1.2.6", {"position": v(46.75, 127.5) * mm});
            skPoint(sketch, "E94.1.2.7", {"position": v(63.5, 92.5) * mm});
            skPoint(sketch, "E94.1.2.8", {"position": v(33, 112.5) * mm});
            skPoint(sketch, "E94.1.2.9", {"position": v(35, 127.5) * mm});
            skLineSegment(sketch, "E94.1.2.10", {"start": v(90.13, 132.5) * mm, "end": v(39.88, 132.5) * mm});
            skLineSegment(sketch, "E94.1.2.11", {"start": v(49.75, 105.5) * mm, "end": v(49.75, 94.5) * mm});
            skLineSegment(sketch, "E94.1.2.12", {"start": v(90.12, 92.5) * mm, "end": v(90.12, 87.5) * mm});
            skLineSegment(sketch, "E94.1.2.13", {"start": v(92.12, 132.5) * mm, "end": v(92.12, 127.5) * mm});
            skLineSegment(sketch, "E94.1.2.14", {"start": v(90.12, 132.5) * mm, "end": v(90.12, 127.5) * mm});
            skLineSegment(sketch, "E94.1.2.15", {"start": v(39.88, 107.5) * mm, "end": v(44.75, 107.5) * mm});
            skLineSegment(sketch, "E94.1.2.16", {"start": v(66.5, 105.5) * mm, "end": v(66.5, 94.5) * mm});
            skPoint(sketch, "E94.1.2.17", {"position": v(33, 127.5) * mm});
            skPoint(sketch, "E94.1.2.18", {"position": v(83.25, 112.5) * mm});
            skPoint(sketch, "E94.1.2.19", {"position": v(66.5, 92.5) * mm});
            skPoint(sketch, "E94.1.2.20", {"position": v(63.5, 112.5) * mm});
            skPoint(sketch, "E94.1.2.21", {"position": v(33, 107.5) * mm});
            skPoint(sketch, "E94.1.2.22", {"position": v(33, 114.5) * mm});
            skLineSegment(sketch, "E94.1.2.23", {"start": v(90.12, 87.5) * mm, "end": v(39.87, 87.5) * mm});
            skLineSegment(sketch, "E94.1.2.24", {"start": v(92.12, 92.5) * mm, "end": v(92.12, 87.5) * mm});
            skLineSegment(sketch, "E94.1.2.25", {"start": v(39.88, 112.5) * mm, "end": v(39.88, 107.5) * mm});
            skLineSegment(sketch, "E94.1.2.26", {"start": v(39.88, 132.5) * mm, "end": v(39.88, 127.5) * mm});
            skLineSegment(sketch, "E94.1.2.27", {"start": v(90.13, 107.5) * mm, "end": v(85.25, 107.5) * mm});
            skLineSegment(sketch, "E94.1.2.28", {"start": v(61.5, 107.5) * mm, "end": v(51.75, 107.5) * mm});
            skPoint(sketch, "E94.1.2.29", {"position": v(63.5, 127.5) * mm});
            skPoint(sketch, "E94.1.2.30", {"position": v(46.75, 92.5) * mm});
            skPoint(sketch, "E94.1.2.31", {"position": v(83.25, 107.5) * mm});
            skPoint(sketch, "E94.1.2.32", {"position": v(63.5, 107.5) * mm});
            skPoint(sketch, "E94.1.2.33", {"position": v(66.5, 127.5) * mm});
            skPoint(sketch, "E94.1.2.34", {"position": v(95, 107.5) * mm});
            skPoint(sketch, "E94.1.2.35", {"position": v(35, 112.5) * mm});
            skLineSegment(sketch, "E94.1.2.36", {"start": v(39.88, 92.5) * mm, "end": v(39.88, 87.5) * mm});
            skLineSegment(sketch, "E94.1.2.37", {"start": v(39.88, 112.5) * mm, "end": v(44.75, 112.5) * mm});
            skLineSegment(sketch, "E94.1.2.38", {"start": v(68.5, 107.5) * mm, "end": v(78.25, 107.5) * mm});
            skLineSegment(sketch, "E94.1.2.39", {"start": v(83.25, 105.5) * mm, "end": v(83.25, 94.5) * mm});
            skLineSegment(sketch, "E94.1.2.40", {"start": v(66.5, 114.5) * mm, "end": v(66.5, 125.5) * mm});
            skLineSegment(sketch, "E94.1.2.41", {"start": v(68.5, 112.5) * mm, "end": v(78.25, 112.5) * mm});
            skLineSegment(sketch, "E94.1.2.42", {"start": v(80.25, 114.5) * mm, "end": v(80.25, 125.5) * mm});
            skLineSegment(sketch, "E94.1.2.43", {"start": v(61.5, 112.5) * mm, "end": v(51.75, 112.5) * mm});
            skLineSegment(sketch, "E94.1.2.44", {"start": v(61.5, 127.5) * mm, "end": v(51.75, 127.5) * mm});
            skLineSegment(sketch, "E94.1.2.45", {"start": v(63.5, 114.5) * mm, "end": v(63.5, 125.5) * mm});
            skLineSegment(sketch, "E94.1.2.46", {"start": v(49.75, 114.5) * mm, "end": v(49.75, 125.5) * mm});
            skLineSegment(sketch, "E94.1.2.47", {"start": v(68.5, 127.5) * mm, "end": v(78.25, 127.5) * mm});
            skPoint(sketch, "E94.1.2.48", {"position": v(80.25, 112.5) * mm});
            skPoint(sketch, "E94.1.2.49", {"position": v(35, 107.5) * mm});
            skPoint(sketch, "E94.1.2.50", {"position": v(46.75, 107.5) * mm});
            skPoint(sketch, "E94.1.2.51", {"position": v(80.25, 107.5) * mm});
            skLineSegment(sketch, "E94.1.2.52", {"start": v(90.12, 127.5) * mm, "end": v(85.25, 127.5) * mm});
            skLineSegment(sketch, "E94.1.2.53", {"start": v(90.12, 112.5) * mm, "end": v(90.12, 107.5) * mm});
            skPoint(sketch, "E94.1.2.54", {"position": v(83.25, 92.5) * mm});
            skPoint(sketch, "E94.1.2.55", {"position": v(49.75, 112.5) * mm});
            skPoint(sketch, "E94.1.2.56", {"position": v(95, 92.5) * mm});
            skLineSegment(sketch, "E94.1.2.57", {"start": v(35, 92.5) * mm, "end": v(105, 92.5) * mm, "construction": true});
            skPoint(sketch, "E94.1.2.58", {"position": v(33, 105.5) * mm});
            skPoint(sketch, "E94.1.2.59", {"position": v(33, 92.5) * mm});
            skPoint(sketch, "E94.1.2.60", {"position": v(80.25, 92.5) * mm});
            skLineSegment(sketch, "E94.1.2.61", {"start": v(39.88, 127.5) * mm, "end": v(44.75, 127.5) * mm});
            skLineSegment(sketch, "E94.1.2.62", {"start": v(63.5, 105.5) * mm, "end": v(63.5, 94.5) * mm});
            skLineSegment(sketch, "E94.1.2.63", {"start": v(92.12, 112.5) * mm, "end": v(92.12, 107.5) * mm});
            skPoint(sketch, "E94.1.2.64", {"position": v(83.25, 127.5) * mm});
            skPoint(sketch, "E94.1.2.65", {"position": v(95, 112.5) * mm});
            skPoint(sketch, "E94.1.2.66", {"position": v(80.25, 127.5) * mm});
            skPoint(sketch, "E94.1.2.67", {"position": v(65, 110) * mm});
            skPoint(sketch, "E94.1.2.68", {"position": v(49.75, 107.5) * mm});
            skLineSegment(sketch, "E94.1.2.69", {"start": v(46.75, 114.5) * mm, "end": v(46.75, 125.5) * mm});
            skLineSegment(sketch, "E94.1.2.70", {"start": v(80.25, 105.5) * mm, "end": v(80.25, 94.5) * mm});
            skLineSegment(sketch, "E94.1.2.71", {"start": v(83.25, 114.5) * mm, "end": v(83.25, 125.5) * mm});
            skPoint(sketch, "E94.1.2.72", {"position": v(95, 127.5) * mm});
            skPoint(sketch, "E94.1.2.73", {"position": v(66.5, 112.5) * mm});
            skPoint(sketch, "E94.1.2.74", {"position": v(33, 94.5) * mm});
            skPoint(sketch, "E94.1.2.75", {"position": v(46.75, 112.5) * mm});
            skPoint(sketch, "E94.1.2.76", {"position": v(66.5, 107.5) * mm});
            skLineSegment(sketch, "E94.1.2.77", {"start": v(90.12, 112.5) * mm, "end": v(90.12, 107.5) * mm});
            skLineSegment(sketch, "E94.1.2.78", {"start": v(68.5, 92.5) * mm, "end": v(78.25, 92.5) * mm});
            skLineSegment(sketch, "E94.1.2.79", {"start": v(90.13, 132.5) * mm, "end": v(90.13, 127.5) * mm});
            skLineSegment(sketch, "E94.1.2.80", {"start": v(90.12, 92.5) * mm, "end": v(90.12, 87.5) * mm});
            skLineSegment(sketch, "E94.1.2.81", {"start": v(39.88, 92.5) * mm, "end": v(39.88, 87.5) * mm});
            skLineSegment(sketch, "E94.1.2.82", {"start": v(39.88, 112.5) * mm, "end": v(39.88, 107.5) * mm});
            skLineSegment(sketch, "E94.1.2.83", {"start": v(61.5, 92.5) * mm, "end": v(51.75, 92.5) * mm});
            skLineSegment(sketch, "E94.1.2.84", {"start": v(39.88, 132.5) * mm, "end": v(39.88, 127.5) * mm});
            skLineSegment(sketch, "E94.1.2.85", {"start": v(39.88, 92.5) * mm, "end": v(44.75, 92.5) * mm});
            skLineSegment(sketch, "E94.1.2.86", {"start": v(90.13, 92.5) * mm, "end": v(85.25, 92.5) * mm});
            skLineSegment(sketch, "E94.1.2.87", {"start": v(90.13, 87.5) * mm, "end": v(92.13, 87.5) * mm});
            skArc(sketch, "E94.1.2.88", {"start": v(80.25, 105.5) * mm, "mid": v(79.66, 106.91) * mm, "end": v(78.25, 107.5) * mm});
            skArc(sketch, "E94.1.2.89", {"start": v(85.25, 127.5) * mm, "mid": v(83.84, 126.91) * mm, "end": v(83.25, 125.5) * mm});
            skArc(sketch, "E94.1.2.90", {"start": v(49.75, 105.5) * mm, "mid": v(50.34, 106.91) * mm, "end": v(51.75, 107.5) * mm});
            skArc(sketch, "E94.1.2.91", {"start": v(83.25, 105.5) * mm, "mid": v(83.84, 106.91) * mm, "end": v(85.25, 107.5) * mm});
            skArc(sketch, "E94.1.2.92", {"start": v(78.25, 92.5) * mm, "mid": v(79.66, 93.09) * mm, "end": v(80.25, 94.5) * mm});
            skLineSegment(sketch, "E94.1.2.93", {"start": v(90.13, 112.5) * mm, "end": v(92.13, 112.5) * mm});
            skArc(sketch, "E94.1.2.94", {"start": v(68.5, 107.5) * mm, "mid": v(67.09, 106.91) * mm, "end": v(66.5, 105.5) * mm});
            skLineSegment(sketch, "E94.1.2.95", {"start": v(90.13, 107.5) * mm, "end": v(92.13, 107.5) * mm});
            skArc(sketch, "E94.1.2.96", {"start": v(46.75, 114.5) * mm, "mid": v(46.16, 113.09) * mm, "end": v(44.75, 112.5) * mm});
            skArc(sketch, "E94.1.2.97", {"start": v(51.75, 127.5) * mm, "mid": v(50.34, 126.91) * mm, "end": v(49.75, 125.5) * mm});
            skArc(sketch, "E94.1.2.98", {"start": v(63.5, 125.5) * mm, "mid": v(62.91, 126.91) * mm, "end": v(61.5, 127.5) * mm});
            skArc(sketch, "E94.1.2.99", {"start": v(61.5, 112.5) * mm, "mid": v(62.91, 113.09) * mm, "end": v(63.5, 114.5) * mm});
            skArc(sketch, "E94.1.2.100", {"start": v(49.75, 114.5) * mm, "mid": v(50.34, 113.09) * mm, "end": v(51.75, 112.5) * mm});
            skArc(sketch, "E94.1.2.101", {"start": v(80.25, 114.5) * mm, "mid": v(79.66, 113.09) * mm, "end": v(78.25, 112.5) * mm});
            skArc(sketch, "E94.1.2.102", {"start": v(78.25, 127.5) * mm, "mid": v(79.66, 126.91) * mm, "end": v(80.25, 125.5) * mm});
            skArc(sketch, "E94.1.2.103", {"start": v(68.5, 112.5) * mm, "mid": v(67.09, 113.09) * mm, "end": v(66.5, 114.5) * mm});
            skArc(sketch, "E94.1.2.104", {"start": v(66.5, 125.5) * mm, "mid": v(67.09, 126.91) * mm, "end": v(68.5, 127.5) * mm});
            skArc(sketch, "E94.1.2.105", {"start": v(66.5, 94.5) * mm, "mid": v(67.09, 93.09) * mm, "end": v(68.5, 92.5) * mm});
            skArc(sketch, "E94.1.2.106", {"start": v(63.5, 94.5) * mm, "mid": v(62.91, 93.09) * mm, "end": v(61.5, 92.5) * mm});
            skArc(sketch, "E94.1.2.107", {"start": v(46.75, 105.5) * mm, "mid": v(46.16, 106.91) * mm, "end": v(44.75, 107.5) * mm});
            skArc(sketch, "E94.1.2.108", {"start": v(61.5, 107.5) * mm, "mid": v(62.91, 106.91) * mm, "end": v(63.5, 105.5) * mm});
            skLineSegment(sketch, "E94.1.2.109", {"start": v(90.13, 132.5) * mm, "end": v(92.12, 132.5) * mm});
            skArc(sketch, "E94.1.2.110", {"start": v(44.75, 127.5) * mm, "mid": v(46.16, 126.91) * mm, "end": v(46.75, 125.5) * mm});
            skArc(sketch, "E94.1.2.111", {"start": v(83.25, 114.5) * mm, "mid": v(83.84, 113.09) * mm, "end": v(85.25, 112.5) * mm});
            skLineSegment(sketch, "E94.1.2.112", {"start": v(90.13, 92.5) * mm, "end": v(92.13, 92.5) * mm});
            skArc(sketch, "E94.1.2.113", {"start": v(51.75, 92.5) * mm, "mid": v(50.34, 93.09) * mm, "end": v(49.75, 94.5) * mm});
            skLineSegment(sketch, "E94.1.2.114", {"start": v(90.13, 127.5) * mm, "end": v(92.12, 127.5) * mm});
            skArc(sketch, "E94.1.2.115", {"start": v(44.75, 92.5) * mm, "mid": v(46.16, 93.09) * mm, "end": v(46.75, 94.5) * mm});
            skArc(sketch, "E94.1.2.116", {"start": v(85.25, 92.5) * mm, "mid": v(83.84, 93.09) * mm, "end": v(83.25, 94.5) * mm});
            skPoint(sketch, "E94.2.0.0", {"position": v(114.75, -17.5) * mm});
            skPoint(sketch, "E94.2.0.1", {"position": v(98, 15.5) * mm});
            skLineSegment(sketch, "E94.2.0.2", {"start": v(155.12, 2.5) * mm, "end": v(150.25, 2.5) * mm});
            skLineSegment(sketch, "E94.2.0.3", {"start": v(111.75, -4.5) * mm, "end": v(111.75, -15.5) * mm});
            skPoint(sketch, "E94.2.0.4", {"position": v(114.75, 17.5) * mm});
            skPoint(sketch, "E94.2.0.5", {"position": v(100, -17.5) * mm});
            skPoint(sketch, "E94.2.0.6", {"position": v(111.75, 17.5) * mm});
            skPoint(sketch, "E94.2.0.7", {"position": v(128.5, -17.5) * mm});
            skPoint(sketch, "E94.2.0.8", {"position": v(98, 2.5) * mm});
            skPoint(sketch, "E94.2.0.9", {"position": v(100, 17.5) * mm});
            skLineSegment(sketch, "E94.2.0.10", {"start": v(155.12, 22.5) * mm, "end": v(104.88, 22.5) * mm});
            skLineSegment(sketch, "E94.2.0.11", {"start": v(114.75, -4.5) * mm, "end": v(114.75, -15.5) * mm});
            skLineSegment(sketch, "E94.2.0.12", {"start": v(155.12, -17.5) * mm, "end": v(155.12, -22.5) * mm});
            skLineSegment(sketch, "E94.2.0.13", {"start": v(157.13, 22.5) * mm, "end": v(157.13, 17.5) * mm});
            skLineSegment(sketch, "E94.2.0.14", {"start": v(155.12, 22.5) * mm, "end": v(155.12, 17.5) * mm});
            skLineSegment(sketch, "E94.2.0.15", {"start": v(104.88, -2.5) * mm, "end": v(109.75, -2.5) * mm});
            skLineSegment(sketch, "E94.2.0.16", {"start": v(131.5, -4.5) * mm, "end": v(131.5, -15.5) * mm});
            skPoint(sketch, "E94.2.0.17", {"position": v(98, 17.5) * mm});
            skPoint(sketch, "E94.2.0.18", {"position": v(148.25, 2.5) * mm});
            skPoint(sketch, "E94.2.0.19", {"position": v(131.5, -17.5) * mm});
            skPoint(sketch, "E94.2.0.20", {"position": v(128.5, 2.5) * mm});
            skPoint(sketch, "E94.2.0.21", {"position": v(98, -2.5) * mm});
            skPoint(sketch, "E94.2.0.22", {"position": v(98, 4.5) * mm});
            skLineSegment(sketch, "E94.2.0.23", {"start": v(155.12, -22.5) * mm, "end": v(104.88, -22.5) * mm});
            skLineSegment(sketch, "E94.2.0.24", {"start": v(157.13, -17.5) * mm, "end": v(157.13, -22.5) * mm});
            skLineSegment(sketch, "E94.2.0.25", {"start": v(104.88, 2.5) * mm, "end": v(104.88, -2.5) * mm});
            skLineSegment(sketch, "E94.2.0.26", {"start": v(104.88, 22.5) * mm, "end": v(104.88, 17.5) * mm});
            skLineSegment(sketch, "E94.2.0.27", {"start": v(155.12, -2.5) * mm, "end": v(150.25, -2.5) * mm});
            skLineSegment(sketch, "E94.2.0.28", {"start": v(126.5, -2.5) * mm, "end": v(116.75, -2.5) * mm});
            skPoint(sketch, "E94.2.0.29", {"position": v(128.5, 17.5) * mm});
            skPoint(sketch, "E94.2.0.30", {"position": v(111.75, -17.5) * mm});
            skPoint(sketch, "E94.2.0.31", {"position": v(148.25, -2.5) * mm});
            skPoint(sketch, "E94.2.0.32", {"position": v(128.5, -2.5) * mm});
            skPoint(sketch, "E94.2.0.33", {"position": v(131.5, 17.5) * mm});
            skPoint(sketch, "E94.2.0.34", {"position": v(160, -2.5) * mm});
            skPoint(sketch, "E94.2.0.35", {"position": v(100, 2.5) * mm});
            skLineSegment(sketch, "E94.2.0.36", {"start": v(104.88, -17.5) * mm, "end": v(104.88, -22.5) * mm});
            skLineSegment(sketch, "E94.2.0.37", {"start": v(104.88, 2.5) * mm, "end": v(109.75, 2.5) * mm});
            skLineSegment(sketch, "E94.2.0.38", {"start": v(133.5, -2.5) * mm, "end": v(143.25, -2.5) * mm});
            skLineSegment(sketch, "E94.2.0.39", {"start": v(148.25, -4.5) * mm, "end": v(148.25, -15.5) * mm});
            skLineSegment(sketch, "E94.2.0.40", {"start": v(131.5, 4.5) * mm, "end": v(131.5, 15.5) * mm});
            skLineSegment(sketch, "E94.2.0.41", {"start": v(133.5, 2.5) * mm, "end": v(143.25, 2.5) * mm});
            skLineSegment(sketch, "E94.2.0.42", {"start": v(145.25, 4.5) * mm, "end": v(145.25, 15.5) * mm});
            skLineSegment(sketch, "E94.2.0.43", {"start": v(126.5, 2.5) * mm, "end": v(116.75, 2.5) * mm});
            skLineSegment(sketch, "E94.2.0.44", {"start": v(126.5, 17.5) * mm, "end": v(116.75, 17.5) * mm});
            skLineSegment(sketch, "E94.2.0.45", {"start": v(128.5, 4.5) * mm, "end": v(128.5, 15.5) * mm});
            skLineSegment(sketch, "E94.2.0.46", {"start": v(114.75, 4.5) * mm, "end": v(114.75, 15.5) * mm});
            skLineSegment(sketch, "E94.2.0.47", {"start": v(133.5, 17.5) * mm, "end": v(143.25, 17.5) * mm});
            skPoint(sketch, "E94.2.0.48", {"position": v(145.25, 2.5) * mm});
            skPoint(sketch, "E94.2.0.49", {"position": v(100, -2.5) * mm});
            skPoint(sketch, "E94.2.0.50", {"position": v(111.75, -2.5) * mm});
            skPoint(sketch, "E94.2.0.51", {"position": v(145.25, -2.5) * mm});
            skLineSegment(sketch, "E94.2.0.52", {"start": v(155.12, 17.5) * mm, "end": v(150.25, 17.5) * mm});
            skLineSegment(sketch, "E94.2.0.53", {"start": v(155.12, 2.5) * mm, "end": v(155.12, -2.5) * mm});
            skPoint(sketch, "E94.2.0.54", {"position": v(148.25, -17.5) * mm});
            skPoint(sketch, "E94.2.0.55", {"position": v(114.75, 2.5) * mm});
            skPoint(sketch, "E94.2.0.56", {"position": v(160, -17.5) * mm});
            skLineSegment(sketch, "E94.2.0.57", {"start": v(100, -17.5) * mm, "end": v(170, -17.5) * mm, "construction": true});
            skPoint(sketch, "E94.2.0.58", {"position": v(98, -4.5) * mm});
            skPoint(sketch, "E94.2.0.59", {"position": v(98, -17.5) * mm});
            skPoint(sketch, "E94.2.0.60", {"position": v(145.25, -17.5) * mm});
            skLineSegment(sketch, "E94.2.0.61", {"start": v(104.88, 17.5) * mm, "end": v(109.75, 17.5) * mm});
            skLineSegment(sketch, "E94.2.0.62", {"start": v(128.5, -4.5) * mm, "end": v(128.5, -15.5) * mm});
            skLineSegment(sketch, "E94.2.0.63", {"start": v(157.13, 2.5) * mm, "end": v(157.13, -2.5) * mm});
            skPoint(sketch, "E94.2.0.64", {"position": v(148.25, 17.5) * mm});
            skPoint(sketch, "E94.2.0.65", {"position": v(160, 2.5) * mm});
            skPoint(sketch, "E94.2.0.66", {"position": v(145.25, 17.5) * mm});
            skPoint(sketch, "E94.2.0.67", {"position": v(130, 0) * mm});
            skPoint(sketch, "E94.2.0.68", {"position": v(114.75, -2.5) * mm});
            skLineSegment(sketch, "E94.2.0.69", {"start": v(111.75, 4.5) * mm, "end": v(111.75, 15.5) * mm});
            skLineSegment(sketch, "E94.2.0.70", {"start": v(145.25, -4.5) * mm, "end": v(145.25, -15.5) * mm});
            skLineSegment(sketch, "E94.2.0.71", {"start": v(148.25, 4.5) * mm, "end": v(148.25, 15.5) * mm});
            skPoint(sketch, "E94.2.0.72", {"position": v(160, 17.5) * mm});
            skPoint(sketch, "E94.2.0.73", {"position": v(131.5, 2.5) * mm});
            skPoint(sketch, "E94.2.0.74", {"position": v(98, -15.5) * mm});
            skPoint(sketch, "E94.2.0.75", {"position": v(111.75, 2.5) * mm});
            skPoint(sketch, "E94.2.0.76", {"position": v(131.5, -2.5) * mm});
            skLineSegment(sketch, "E94.2.0.77", {"start": v(155.12, 2.5) * mm, "end": v(155.12, -2.5) * mm});
            skLineSegment(sketch, "E94.2.0.78", {"start": v(133.5, -17.5) * mm, "end": v(143.25, -17.5) * mm});
            skLineSegment(sketch, "E94.2.0.79", {"start": v(155.12, 22.5) * mm, "end": v(155.12, 17.5) * mm});
            skLineSegment(sketch, "E94.2.0.80", {"start": v(155.12, -17.5) * mm, "end": v(155.12, -22.5) * mm});
            skLineSegment(sketch, "E94.2.0.81", {"start": v(104.88, -17.5) * mm, "end": v(104.88, -22.5) * mm});
            skLineSegment(sketch, "E94.2.0.82", {"start": v(104.88, 2.5) * mm, "end": v(104.88, -2.5) * mm});
            skLineSegment(sketch, "E94.2.0.83", {"start": v(126.5, -17.5) * mm, "end": v(116.75, -17.5) * mm});
            skLineSegment(sketch, "E94.2.0.84", {"start": v(104.88, 22.5) * mm, "end": v(104.88, 17.5) * mm});
            skLineSegment(sketch, "E94.2.0.85", {"start": v(104.88, -17.5) * mm, "end": v(109.75, -17.5) * mm});
            skLineSegment(sketch, "E94.2.0.86", {"start": v(155.12, -17.5) * mm, "end": v(150.25, -17.5) * mm});
            skLineSegment(sketch, "E94.2.0.87", {"start": v(155.12, -22.5) * mm, "end": v(157.13, -22.5) * mm});
            skArc(sketch, "E94.2.0.88", {"start": v(145.25, -4.5) * mm, "mid": v(144.66, -3.09) * mm, "end": v(143.25, -2.5) * mm});
            skArc(sketch, "E94.2.0.89", {"start": v(150.25, 17.5) * mm, "mid": v(148.84, 16.91) * mm, "end": v(148.25, 15.5) * mm});
            skArc(sketch, "E94.2.0.90", {"start": v(114.75, -4.5) * mm, "mid": v(115.34, -3.09) * mm, "end": v(116.75, -2.5) * mm});
            skArc(sketch, "E94.2.0.91", {"start": v(148.25, -4.5) * mm, "mid": v(148.84, -3.09) * mm, "end": v(150.25, -2.5) * mm});
            skArc(sketch, "E94.2.0.92", {"start": v(143.25, -17.5) * mm, "mid": v(144.66, -16.91) * mm, "end": v(145.25, -15.5) * mm});
            skLineSegment(sketch, "E94.2.0.93", {"start": v(155.12, 2.5) * mm, "end": v(157.13, 2.5) * mm});
            skArc(sketch, "E94.2.0.94", {"start": v(133.5, -2.5) * mm, "mid": v(132.09, -3.09) * mm, "end": v(131.5, -4.5) * mm});
            skLineSegment(sketch, "E94.2.0.95", {"start": v(155.12, -2.5) * mm, "end": v(157.13, -2.5) * mm});
            skArc(sketch, "E94.2.0.96", {"start": v(111.75, 4.5) * mm, "mid": v(111.16, 3.09) * mm, "end": v(109.75, 2.5) * mm});
            skArc(sketch, "E94.2.0.97", {"start": v(116.75, 17.5) * mm, "mid": v(115.34, 16.91) * mm, "end": v(114.75, 15.5) * mm});
            skArc(sketch, "E94.2.0.98", {"start": v(128.5, 15.5) * mm, "mid": v(127.91, 16.91) * mm, "end": v(126.5, 17.5) * mm});
            skArc(sketch, "E94.2.0.99", {"start": v(126.5, 2.5) * mm, "mid": v(127.91, 3.09) * mm, "end": v(128.5, 4.5) * mm});
            skArc(sketch, "E94.2.0.100", {"start": v(114.75, 4.5) * mm, "mid": v(115.34, 3.09) * mm, "end": v(116.75, 2.5) * mm});
            skArc(sketch, "E94.2.0.101", {"start": v(145.25, 4.5) * mm, "mid": v(144.66, 3.09) * mm, "end": v(143.25, 2.5) * mm});
            skArc(sketch, "E94.2.0.102", {"start": v(143.25, 17.5) * mm, "mid": v(144.66, 16.91) * mm, "end": v(145.25, 15.5) * mm});
            skArc(sketch, "E94.2.0.103", {"start": v(133.5, 2.5) * mm, "mid": v(132.09, 3.09) * mm, "end": v(131.5, 4.5) * mm});
            skArc(sketch, "E94.2.0.104", {"start": v(131.5, 15.5) * mm, "mid": v(132.09, 16.91) * mm, "end": v(133.5, 17.5) * mm});
            skArc(sketch, "E94.2.0.105", {"start": v(131.5, -15.5) * mm, "mid": v(132.09, -16.91) * mm, "end": v(133.5, -17.5) * mm});
            skArc(sketch, "E94.2.0.106", {"start": v(128.5, -15.5) * mm, "mid": v(127.91, -16.91) * mm, "end": v(126.5, -17.5) * mm});
            skArc(sketch, "E94.2.0.107", {"start": v(111.75, -4.5) * mm, "mid": v(111.16, -3.09) * mm, "end": v(109.75, -2.5) * mm});
            skArc(sketch, "E94.2.0.108", {"start": v(126.5, -2.5) * mm, "mid": v(127.91, -3.09) * mm, "end": v(128.5, -4.5) * mm});
            skLineSegment(sketch, "E94.2.0.109", {"start": v(155.12, 22.5) * mm, "end": v(157.13, 22.5) * mm});
            skArc(sketch, "E94.2.0.110", {"start": v(109.75, 17.5) * mm, "mid": v(111.16, 16.91) * mm, "end": v(111.75, 15.5) * mm});
            skArc(sketch, "E94.2.0.111", {"start": v(148.25, 4.5) * mm, "mid": v(148.84, 3.09) * mm, "end": v(150.25, 2.5) * mm});
            skLineSegment(sketch, "E94.2.0.112", {"start": v(155.12, -17.5) * mm, "end": v(157.13, -17.5) * mm});
            skArc(sketch, "E94.2.0.113", {"start": v(116.75, -17.5) * mm, "mid": v(115.34, -16.91) * mm, "end": v(114.75, -15.5) * mm});
            skLineSegment(sketch, "E94.2.0.114", {"start": v(155.12, 17.5) * mm, "end": v(157.13, 17.5) * mm});
            skArc(sketch, "E94.2.0.115", {"start": v(109.75, -17.5) * mm, "mid": v(111.16, -16.91) * mm, "end": v(111.75, -15.5) * mm});
            skArc(sketch, "E94.2.0.116", {"start": v(150.25, -17.5) * mm, "mid": v(148.84, -16.91) * mm, "end": v(148.25, -15.5) * mm});
            skPoint(sketch, "E94.2.1.0", {"position": v(114.75, 37.5) * mm});
            skPoint(sketch, "E94.2.1.1", {"position": v(98, 70.5) * mm});
            skLineSegment(sketch, "E94.2.1.2", {"start": v(155.12, 57.5) * mm, "end": v(150.25, 57.5) * mm});
            skLineSegment(sketch, "E94.2.1.3", {"start": v(111.75, 50.5) * mm, "end": v(111.75, 39.5) * mm});
            skPoint(sketch, "E94.2.1.4", {"position": v(114.75, 72.5) * mm});
            skPoint(sketch, "E94.2.1.5", {"position": v(100, 37.5) * mm});
            skPoint(sketch, "E94.2.1.6", {"position": v(111.75, 72.5) * mm});
            skPoint(sketch, "E94.2.1.7", {"position": v(128.5, 37.5) * mm});
            skPoint(sketch, "E94.2.1.8", {"position": v(98, 57.5) * mm});
            skPoint(sketch, "E94.2.1.9", {"position": v(100, 72.5) * mm});
            skLineSegment(sketch, "E94.2.1.10", {"start": v(155.12, 77.5) * mm, "end": v(104.88, 77.5) * mm});
            skLineSegment(sketch, "E94.2.1.11", {"start": v(114.75, 50.5) * mm, "end": v(114.75, 39.5) * mm});
            skLineSegment(sketch, "E94.2.1.12", {"start": v(155.12, 37.5) * mm, "end": v(155.12, 32.5) * mm});
            skLineSegment(sketch, "E94.2.1.13", {"start": v(157.13, 77.5) * mm, "end": v(157.13, 72.5) * mm});
            skLineSegment(sketch, "E94.2.1.14", {"start": v(155.12, 77.5) * mm, "end": v(155.12, 72.5) * mm});
            skLineSegment(sketch, "E94.2.1.15", {"start": v(104.88, 52.5) * mm, "end": v(109.75, 52.5) * mm});
            skLineSegment(sketch, "E94.2.1.16", {"start": v(131.5, 50.5) * mm, "end": v(131.5, 39.5) * mm});
            skPoint(sketch, "E94.2.1.17", {"position": v(98, 72.5) * mm});
            skPoint(sketch, "E94.2.1.18", {"position": v(148.25, 57.5) * mm});
            skPoint(sketch, "E94.2.1.19", {"position": v(131.5, 37.5) * mm});
            skPoint(sketch, "E94.2.1.20", {"position": v(128.5, 57.5) * mm});
            skPoint(sketch, "E94.2.1.21", {"position": v(98, 52.5) * mm});
            skPoint(sketch, "E94.2.1.22", {"position": v(98, 59.5) * mm});
            skLineSegment(sketch, "E94.2.1.23", {"start": v(155.12, 32.5) * mm, "end": v(104.88, 32.5) * mm});
            skLineSegment(sketch, "E94.2.1.24", {"start": v(157.13, 37.5) * mm, "end": v(157.13, 32.5) * mm});
            skLineSegment(sketch, "E94.2.1.25", {"start": v(104.88, 57.5) * mm, "end": v(104.88, 52.5) * mm});
            skLineSegment(sketch, "E94.2.1.26", {"start": v(104.88, 77.5) * mm, "end": v(104.88, 72.5) * mm});
            skLineSegment(sketch, "E94.2.1.27", {"start": v(155.12, 52.5) * mm, "end": v(150.25, 52.5) * mm});
            skLineSegment(sketch, "E94.2.1.28", {"start": v(126.5, 52.5) * mm, "end": v(116.75, 52.5) * mm});
            skPoint(sketch, "E94.2.1.29", {"position": v(128.5, 72.5) * mm});
            skPoint(sketch, "E94.2.1.30", {"position": v(111.75, 37.5) * mm});
            skPoint(sketch, "E94.2.1.31", {"position": v(148.25, 52.5) * mm});
            skPoint(sketch, "E94.2.1.32", {"position": v(128.5, 52.5) * mm});
            skPoint(sketch, "E94.2.1.33", {"position": v(131.5, 72.5) * mm});
            skPoint(sketch, "E94.2.1.34", {"position": v(160, 52.5) * mm});
            skPoint(sketch, "E94.2.1.35", {"position": v(100, 57.5) * mm});
            skLineSegment(sketch, "E94.2.1.36", {"start": v(104.88, 37.5) * mm, "end": v(104.88, 32.5) * mm});
            skLineSegment(sketch, "E94.2.1.37", {"start": v(104.88, 57.5) * mm, "end": v(109.75, 57.5) * mm});
            skLineSegment(sketch, "E94.2.1.38", {"start": v(133.5, 52.5) * mm, "end": v(143.25, 52.5) * mm});
            skLineSegment(sketch, "E94.2.1.39", {"start": v(148.25, 50.5) * mm, "end": v(148.25, 39.5) * mm});
            skLineSegment(sketch, "E94.2.1.40", {"start": v(131.5, 59.5) * mm, "end": v(131.5, 70.5) * mm});
            skLineSegment(sketch, "E94.2.1.41", {"start": v(133.5, 57.5) * mm, "end": v(143.25, 57.5) * mm});
            skLineSegment(sketch, "E94.2.1.42", {"start": v(145.25, 59.5) * mm, "end": v(145.25, 70.5) * mm});
            skLineSegment(sketch, "E94.2.1.43", {"start": v(126.5, 57.5) * mm, "end": v(116.75, 57.5) * mm});
            skLineSegment(sketch, "E94.2.1.44", {"start": v(126.5, 72.5) * mm, "end": v(116.75, 72.5) * mm});
            skLineSegment(sketch, "E94.2.1.45", {"start": v(128.5, 59.5) * mm, "end": v(128.5, 70.5) * mm});
            skLineSegment(sketch, "E94.2.1.46", {"start": v(114.75, 59.5) * mm, "end": v(114.75, 70.5) * mm});
            skLineSegment(sketch, "E94.2.1.47", {"start": v(133.5, 72.5) * mm, "end": v(143.25, 72.5) * mm});
            skPoint(sketch, "E94.2.1.48", {"position": v(145.25, 57.5) * mm});
            skPoint(sketch, "E94.2.1.49", {"position": v(100, 52.5) * mm});
            skPoint(sketch, "E94.2.1.50", {"position": v(111.75, 52.5) * mm});
            skPoint(sketch, "E94.2.1.51", {"position": v(145.25, 52.5) * mm});
            skLineSegment(sketch, "E94.2.1.52", {"start": v(155.12, 72.5) * mm, "end": v(150.25, 72.5) * mm});
            skLineSegment(sketch, "E94.2.1.53", {"start": v(155.12, 57.5) * mm, "end": v(155.12, 52.5) * mm});
            skPoint(sketch, "E94.2.1.54", {"position": v(148.25, 37.5) * mm});
            skPoint(sketch, "E94.2.1.55", {"position": v(114.75, 57.5) * mm});
            skPoint(sketch, "E94.2.1.56", {"position": v(160, 37.5) * mm});
            skLineSegment(sketch, "E94.2.1.57", {"start": v(100, 37.5) * mm, "end": v(170, 37.5) * mm, "construction": true});
            skPoint(sketch, "E94.2.1.58", {"position": v(98, 50.5) * mm});
            skPoint(sketch, "E94.2.1.59", {"position": v(98, 37.5) * mm});
            skPoint(sketch, "E94.2.1.60", {"position": v(145.25, 37.5) * mm});
            skLineSegment(sketch, "E94.2.1.61", {"start": v(104.88, 72.5) * mm, "end": v(109.75, 72.5) * mm});
            skLineSegment(sketch, "E94.2.1.62", {"start": v(128.5, 50.5) * mm, "end": v(128.5, 39.5) * mm});
            skLineSegment(sketch, "E94.2.1.63", {"start": v(157.13, 57.5) * mm, "end": v(157.13, 52.5) * mm});
            skPoint(sketch, "E94.2.1.64", {"position": v(148.25, 72.5) * mm});
            skPoint(sketch, "E94.2.1.65", {"position": v(160, 57.5) * mm});
            skPoint(sketch, "E94.2.1.66", {"position": v(145.25, 72.5) * mm});
            skPoint(sketch, "E94.2.1.67", {"position": v(130, 55) * mm});
            skPoint(sketch, "E94.2.1.68", {"position": v(114.75, 52.5) * mm});
            skLineSegment(sketch, "E94.2.1.69", {"start": v(111.75, 59.5) * mm, "end": v(111.75, 70.5) * mm});
            skLineSegment(sketch, "E94.2.1.70", {"start": v(145.25, 50.5) * mm, "end": v(145.25, 39.5) * mm});
            skLineSegment(sketch, "E94.2.1.71", {"start": v(148.25, 59.5) * mm, "end": v(148.25, 70.5) * mm});
            skPoint(sketch, "E94.2.1.72", {"position": v(160, 72.5) * mm});
            skPoint(sketch, "E94.2.1.73", {"position": v(131.5, 57.5) * mm});
            skPoint(sketch, "E94.2.1.74", {"position": v(98, 39.5) * mm});
            skPoint(sketch, "E94.2.1.75", {"position": v(111.75, 57.5) * mm});
            skPoint(sketch, "E94.2.1.76", {"position": v(131.5, 52.5) * mm});
            skLineSegment(sketch, "E94.2.1.77", {"start": v(155.12, 57.5) * mm, "end": v(155.12, 52.5) * mm});
            skLineSegment(sketch, "E94.2.1.78", {"start": v(133.5, 37.5) * mm, "end": v(143.25, 37.5) * mm});
            skLineSegment(sketch, "E94.2.1.79", {"start": v(155.12, 77.5) * mm, "end": v(155.12, 72.5) * mm});
            skLineSegment(sketch, "E94.2.1.80", {"start": v(155.12, 37.5) * mm, "end": v(155.12, 32.5) * mm});
            skLineSegment(sketch, "E94.2.1.81", {"start": v(104.88, 37.5) * mm, "end": v(104.88, 32.5) * mm});
            skLineSegment(sketch, "E94.2.1.82", {"start": v(104.88, 57.5) * mm, "end": v(104.88, 52.5) * mm});
            skLineSegment(sketch, "E94.2.1.83", {"start": v(126.5, 37.5) * mm, "end": v(116.75, 37.5) * mm});
            skLineSegment(sketch, "E94.2.1.84", {"start": v(104.88, 77.5) * mm, "end": v(104.88, 72.5) * mm});
            skLineSegment(sketch, "E94.2.1.85", {"start": v(104.88, 37.5) * mm, "end": v(109.75, 37.5) * mm});
            skLineSegment(sketch, "E94.2.1.86", {"start": v(155.12, 37.5) * mm, "end": v(150.25, 37.5) * mm});
            skLineSegment(sketch, "E94.2.1.87", {"start": v(155.12, 32.5) * mm, "end": v(157.13, 32.5) * mm});
            skArc(sketch, "E94.2.1.88", {"start": v(145.25, 50.5) * mm, "mid": v(144.66, 51.91) * mm, "end": v(143.25, 52.5) * mm});
            skArc(sketch, "E94.2.1.89", {"start": v(150.25, 72.5) * mm, "mid": v(148.84, 71.91) * mm, "end": v(148.25, 70.5) * mm});
            skArc(sketch, "E94.2.1.90", {"start": v(114.75, 50.5) * mm, "mid": v(115.34, 51.91) * mm, "end": v(116.75, 52.5) * mm});
            skArc(sketch, "E94.2.1.91", {"start": v(148.25, 50.5) * mm, "mid": v(148.84, 51.91) * mm, "end": v(150.25, 52.5) * mm});
            skArc(sketch, "E94.2.1.92", {"start": v(143.25, 37.5) * mm, "mid": v(144.66, 38.09) * mm, "end": v(145.25, 39.5) * mm});
            skLineSegment(sketch, "E94.2.1.93", {"start": v(155.12, 57.5) * mm, "end": v(157.13, 57.5) * mm});
            skArc(sketch, "E94.2.1.94", {"start": v(133.5, 52.5) * mm, "mid": v(132.09, 51.91) * mm, "end": v(131.5, 50.5) * mm});
            skLineSegment(sketch, "E94.2.1.95", {"start": v(155.12, 52.5) * mm, "end": v(157.13, 52.5) * mm});
            skArc(sketch, "E94.2.1.96", {"start": v(111.75, 59.5) * mm, "mid": v(111.16, 58.09) * mm, "end": v(109.75, 57.5) * mm});
            skArc(sketch, "E94.2.1.97", {"start": v(116.75, 72.5) * mm, "mid": v(115.34, 71.91) * mm, "end": v(114.75, 70.5) * mm});
            skArc(sketch, "E94.2.1.98", {"start": v(128.5, 70.5) * mm, "mid": v(127.91, 71.91) * mm, "end": v(126.5, 72.5) * mm});
            skArc(sketch, "E94.2.1.99", {"start": v(126.5, 57.5) * mm, "mid": v(127.91, 58.09) * mm, "end": v(128.5, 59.5) * mm});
            skArc(sketch, "E94.2.1.100", {"start": v(114.75, 59.5) * mm, "mid": v(115.34, 58.09) * mm, "end": v(116.75, 57.5) * mm});
            skArc(sketch, "E94.2.1.101", {"start": v(145.25, 59.5) * mm, "mid": v(144.66, 58.09) * mm, "end": v(143.25, 57.5) * mm});
            skArc(sketch, "E94.2.1.102", {"start": v(143.25, 72.5) * mm, "mid": v(144.66, 71.91) * mm, "end": v(145.25, 70.5) * mm});
            skArc(sketch, "E94.2.1.103", {"start": v(133.5, 57.5) * mm, "mid": v(132.09, 58.09) * mm, "end": v(131.5, 59.5) * mm});
            skArc(sketch, "E94.2.1.104", {"start": v(131.5, 70.5) * mm, "mid": v(132.09, 71.91) * mm, "end": v(133.5, 72.5) * mm});
            skArc(sketch, "E94.2.1.105", {"start": v(131.5, 39.5) * mm, "mid": v(132.09, 38.09) * mm, "end": v(133.5, 37.5) * mm});
            skArc(sketch, "E94.2.1.106", {"start": v(128.5, 39.5) * mm, "mid": v(127.91, 38.09) * mm, "end": v(126.5, 37.5) * mm});
            skArc(sketch, "E94.2.1.107", {"start": v(111.75, 50.5) * mm, "mid": v(111.16, 51.91) * mm, "end": v(109.75, 52.5) * mm});
            skArc(sketch, "E94.2.1.108", {"start": v(126.5, 52.5) * mm, "mid": v(127.91, 51.91) * mm, "end": v(128.5, 50.5) * mm});
            skLineSegment(sketch, "E94.2.1.109", {"start": v(155.12, 77.5) * mm, "end": v(157.13, 77.5) * mm});
            skArc(sketch, "E94.2.1.110", {"start": v(109.75, 72.5) * mm, "mid": v(111.16, 71.91) * mm, "end": v(111.75, 70.5) * mm});
            skArc(sketch, "E94.2.1.111", {"start": v(148.25, 59.5) * mm, "mid": v(148.84, 58.09) * mm, "end": v(150.25, 57.5) * mm});
            skLineSegment(sketch, "E94.2.1.112", {"start": v(155.12, 37.5) * mm, "end": v(157.13, 37.5) * mm});
            skArc(sketch, "E94.2.1.113", {"start": v(116.75, 37.5) * mm, "mid": v(115.34, 38.09) * mm, "end": v(114.75, 39.5) * mm});
            skLineSegment(sketch, "E94.2.1.114", {"start": v(155.12, 72.5) * mm, "end": v(157.13, 72.5) * mm});
            skArc(sketch, "E94.2.1.115", {"start": v(109.75, 37.5) * mm, "mid": v(111.16, 38.09) * mm, "end": v(111.75, 39.5) * mm});
            skArc(sketch, "E94.2.1.116", {"start": v(150.25, 37.5) * mm, "mid": v(148.84, 38.09) * mm, "end": v(148.25, 39.5) * mm});
            skPoint(sketch, "E94.2.2.0", {"position": v(114.75, 92.5) * mm});
            skPoint(sketch, "E94.2.2.1", {"position": v(98, 125.5) * mm});
            skLineSegment(sketch, "E94.2.2.2", {"start": v(155.12, 112.5) * mm, "end": v(150.25, 112.5) * mm});
            skLineSegment(sketch, "E94.2.2.3", {"start": v(111.75, 105.5) * mm, "end": v(111.75, 94.5) * mm});
            skPoint(sketch, "E94.2.2.4", {"position": v(114.75, 127.5) * mm});
            skPoint(sketch, "E94.2.2.5", {"position": v(100, 92.5) * mm});
            skPoint(sketch, "E94.2.2.6", {"position": v(111.75, 127.5) * mm});
            skPoint(sketch, "E94.2.2.7", {"position": v(128.5, 92.5) * mm});
            skPoint(sketch, "E94.2.2.8", {"position": v(98, 112.5) * mm});
            skPoint(sketch, "E94.2.2.9", {"position": v(100, 127.5) * mm});
            skLineSegment(sketch, "E94.2.2.10", {"start": v(155.12, 132.5) * mm, "end": v(104.88, 132.5) * mm});
            skLineSegment(sketch, "E94.2.2.11", {"start": v(114.75, 105.5) * mm, "end": v(114.75, 94.5) * mm});
            skLineSegment(sketch, "E94.2.2.12", {"start": v(155.12, 92.5) * mm, "end": v(155.12, 87.5) * mm});
            skLineSegment(sketch, "E94.2.2.13", {"start": v(157.13, 132.5) * mm, "end": v(157.13, 127.5) * mm});
            skLineSegment(sketch, "E94.2.2.14", {"start": v(155.12, 132.5) * mm, "end": v(155.12, 127.5) * mm});
            skLineSegment(sketch, "E94.2.2.15", {"start": v(104.88, 107.5) * mm, "end": v(109.75, 107.5) * mm});
            skLineSegment(sketch, "E94.2.2.16", {"start": v(131.5, 105.5) * mm, "end": v(131.5, 94.5) * mm});
            skPoint(sketch, "E94.2.2.17", {"position": v(98, 127.5) * mm});
            skPoint(sketch, "E94.2.2.18", {"position": v(148.25, 112.5) * mm});
            skPoint(sketch, "E94.2.2.19", {"position": v(131.5, 92.5) * mm});
            skPoint(sketch, "E94.2.2.20", {"position": v(128.5, 112.5) * mm});
            skPoint(sketch, "E94.2.2.21", {"position": v(98, 107.5) * mm});
            skPoint(sketch, "E94.2.2.22", {"position": v(98, 114.5) * mm});
            skLineSegment(sketch, "E94.2.2.23", {"start": v(155.12, 87.5) * mm, "end": v(104.88, 87.5) * mm});
            skLineSegment(sketch, "E94.2.2.24", {"start": v(157.13, 92.5) * mm, "end": v(157.13, 87.5) * mm});
            skLineSegment(sketch, "E94.2.2.25", {"start": v(104.88, 112.5) * mm, "end": v(104.88, 107.5) * mm});
            skLineSegment(sketch, "E94.2.2.26", {"start": v(104.88, 132.5) * mm, "end": v(104.88, 127.5) * mm});
            skLineSegment(sketch, "E94.2.2.27", {"start": v(155.12, 107.5) * mm, "end": v(150.25, 107.5) * mm});
            skLineSegment(sketch, "E94.2.2.28", {"start": v(126.5, 107.5) * mm, "end": v(116.75, 107.5) * mm});
            skPoint(sketch, "E94.2.2.29", {"position": v(128.5, 127.5) * mm});
            skPoint(sketch, "E94.2.2.30", {"position": v(111.75, 92.5) * mm});
            skPoint(sketch, "E94.2.2.31", {"position": v(148.25, 107.5) * mm});
            skPoint(sketch, "E94.2.2.32", {"position": v(128.5, 107.5) * mm});
            skPoint(sketch, "E94.2.2.33", {"position": v(131.5, 127.5) * mm});
            skPoint(sketch, "E94.2.2.34", {"position": v(160, 107.5) * mm});
            skPoint(sketch, "E94.2.2.35", {"position": v(100, 112.5) * mm});
            skLineSegment(sketch, "E94.2.2.36", {"start": v(104.88, 92.5) * mm, "end": v(104.88, 87.5) * mm});
            skLineSegment(sketch, "E94.2.2.37", {"start": v(104.88, 112.5) * mm, "end": v(109.75, 112.5) * mm});
            skLineSegment(sketch, "E94.2.2.38", {"start": v(133.5, 107.5) * mm, "end": v(143.25, 107.5) * mm});
            skLineSegment(sketch, "E94.2.2.39", {"start": v(148.25, 105.5) * mm, "end": v(148.25, 94.5) * mm});
            skLineSegment(sketch, "E94.2.2.40", {"start": v(131.5, 114.5) * mm, "end": v(131.5, 125.5) * mm});
            skLineSegment(sketch, "E94.2.2.41", {"start": v(133.5, 112.5) * mm, "end": v(143.25, 112.5) * mm});
            skLineSegment(sketch, "E94.2.2.42", {"start": v(145.25, 114.5) * mm, "end": v(145.25, 125.5) * mm});
            skLineSegment(sketch, "E94.2.2.43", {"start": v(126.5, 112.5) * mm, "end": v(116.75, 112.5) * mm});
            skLineSegment(sketch, "E94.2.2.44", {"start": v(126.5, 127.5) * mm, "end": v(116.75, 127.5) * mm});
            skLineSegment(sketch, "E94.2.2.45", {"start": v(128.5, 114.5) * mm, "end": v(128.5, 125.5) * mm});
            skLineSegment(sketch, "E94.2.2.46", {"start": v(114.75, 114.5) * mm, "end": v(114.75, 125.5) * mm});
            skLineSegment(sketch, "E94.2.2.47", {"start": v(133.5, 127.5) * mm, "end": v(143.25, 127.5) * mm});
            skPoint(sketch, "E94.2.2.48", {"position": v(145.25, 112.5) * mm});
            skPoint(sketch, "E94.2.2.49", {"position": v(100, 107.5) * mm});
            skPoint(sketch, "E94.2.2.50", {"position": v(111.75, 107.5) * mm});
            skPoint(sketch, "E94.2.2.51", {"position": v(145.25, 107.5) * mm});
            skLineSegment(sketch, "E94.2.2.52", {"start": v(155.12, 127.5) * mm, "end": v(150.25, 127.5) * mm});
            skLineSegment(sketch, "E94.2.2.53", {"start": v(155.12, 112.5) * mm, "end": v(155.12, 107.5) * mm});
            skPoint(sketch, "E94.2.2.54", {"position": v(148.25, 92.5) * mm});
            skPoint(sketch, "E94.2.2.55", {"position": v(114.75, 112.5) * mm});
            skPoint(sketch, "E94.2.2.56", {"position": v(160, 92.5) * mm});
            skLineSegment(sketch, "E94.2.2.57", {"start": v(100, 92.5) * mm, "end": v(170, 92.5) * mm, "construction": true});
            skPoint(sketch, "E94.2.2.58", {"position": v(98, 105.5) * mm});
            skPoint(sketch, "E94.2.2.59", {"position": v(98, 92.5) * mm});
            skPoint(sketch, "E94.2.2.60", {"position": v(145.25, 92.5) * mm});
            skLineSegment(sketch, "E94.2.2.61", {"start": v(104.88, 127.5) * mm, "end": v(109.75, 127.5) * mm});
            skLineSegment(sketch, "E94.2.2.62", {"start": v(128.5, 105.5) * mm, "end": v(128.5, 94.5) * mm});
            skLineSegment(sketch, "E94.2.2.63", {"start": v(157.13, 112.5) * mm, "end": v(157.13, 107.5) * mm});
            skPoint(sketch, "E94.2.2.64", {"position": v(148.25, 127.5) * mm});
            skPoint(sketch, "E94.2.2.65", {"position": v(160, 112.5) * mm});
            skPoint(sketch, "E94.2.2.66", {"position": v(145.25, 127.5) * mm});
            skPoint(sketch, "E94.2.2.67", {"position": v(130, 110) * mm});
            skPoint(sketch, "E94.2.2.68", {"position": v(114.75, 107.5) * mm});
            skLineSegment(sketch, "E94.2.2.69", {"start": v(111.75, 114.5) * mm, "end": v(111.75, 125.5) * mm});
            skLineSegment(sketch, "E94.2.2.70", {"start": v(145.25, 105.5) * mm, "end": v(145.25, 94.5) * mm});
            skLineSegment(sketch, "E94.2.2.71", {"start": v(148.25, 114.5) * mm, "end": v(148.25, 125.5) * mm});
            skPoint(sketch, "E94.2.2.72", {"position": v(160, 127.5) * mm});
            skPoint(sketch, "E94.2.2.73", {"position": v(131.5, 112.5) * mm});
            skPoint(sketch, "E94.2.2.74", {"position": v(98, 94.5) * mm});
            skPoint(sketch, "E94.2.2.75", {"position": v(111.75, 112.5) * mm});
            skPoint(sketch, "E94.2.2.76", {"position": v(131.5, 107.5) * mm});
            skLineSegment(sketch, "E94.2.2.77", {"start": v(155.12, 112.5) * mm, "end": v(155.12, 107.5) * mm});
            skLineSegment(sketch, "E94.2.2.78", {"start": v(133.5, 92.5) * mm, "end": v(143.25, 92.5) * mm});
            skLineSegment(sketch, "E94.2.2.79", {"start": v(155.12, 132.5) * mm, "end": v(155.12, 127.5) * mm});
            skLineSegment(sketch, "E94.2.2.80", {"start": v(155.12, 92.5) * mm, "end": v(155.12, 87.5) * mm});
            skLineSegment(sketch, "E94.2.2.81", {"start": v(104.88, 92.5) * mm, "end": v(104.88, 87.5) * mm});
            skLineSegment(sketch, "E94.2.2.82", {"start": v(104.88, 112.5) * mm, "end": v(104.88, 107.5) * mm});
            skLineSegment(sketch, "E94.2.2.83", {"start": v(126.5, 92.5) * mm, "end": v(116.75, 92.5) * mm});
            skLineSegment(sketch, "E94.2.2.84", {"start": v(104.88, 132.5) * mm, "end": v(104.88, 127.5) * mm});
            skLineSegment(sketch, "E94.2.2.85", {"start": v(104.88, 92.5) * mm, "end": v(109.75, 92.5) * mm});
            skLineSegment(sketch, "E94.2.2.86", {"start": v(155.12, 92.5) * mm, "end": v(150.25, 92.5) * mm});
            skLineSegment(sketch, "E94.2.2.87", {"start": v(155.12, 87.5) * mm, "end": v(157.13, 87.5) * mm});
            skArc(sketch, "E94.2.2.88", {"start": v(145.25, 105.5) * mm, "mid": v(144.66, 106.91) * mm, "end": v(143.25, 107.5) * mm});
            skArc(sketch, "E94.2.2.89", {"start": v(150.25, 127.5) * mm, "mid": v(148.84, 126.91) * mm, "end": v(148.25, 125.5) * mm});
            skArc(sketch, "E94.2.2.90", {"start": v(114.75, 105.5) * mm, "mid": v(115.34, 106.91) * mm, "end": v(116.75, 107.5) * mm});
            skArc(sketch, "E94.2.2.91", {"start": v(148.25, 105.5) * mm, "mid": v(148.84, 106.91) * mm, "end": v(150.25, 107.5) * mm});
            skArc(sketch, "E94.2.2.92", {"start": v(143.25, 92.5) * mm, "mid": v(144.66, 93.09) * mm, "end": v(145.25, 94.5) * mm});
            skLineSegment(sketch, "E94.2.2.93", {"start": v(155.12, 112.5) * mm, "end": v(157.13, 112.5) * mm});
            skArc(sketch, "E94.2.2.94", {"start": v(133.5, 107.5) * mm, "mid": v(132.09, 106.91) * mm, "end": v(131.5, 105.5) * mm});
            skLineSegment(sketch, "E94.2.2.95", {"start": v(155.12, 107.5) * mm, "end": v(157.13, 107.5) * mm});
            skArc(sketch, "E94.2.2.96", {"start": v(111.75, 114.5) * mm, "mid": v(111.16, 113.09) * mm, "end": v(109.75, 112.5) * mm});
            skArc(sketch, "E94.2.2.97", {"start": v(116.75, 127.5) * mm, "mid": v(115.34, 126.91) * mm, "end": v(114.75, 125.5) * mm});
            skArc(sketch, "E94.2.2.98", {"start": v(128.5, 125.5) * mm, "mid": v(127.91, 126.91) * mm, "end": v(126.5, 127.5) * mm});
            skArc(sketch, "E94.2.2.99", {"start": v(126.5, 112.5) * mm, "mid": v(127.91, 113.09) * mm, "end": v(128.5, 114.5) * mm});
            skArc(sketch, "E94.2.2.100", {"start": v(114.75, 114.5) * mm, "mid": v(115.34, 113.09) * mm, "end": v(116.75, 112.5) * mm});
            skArc(sketch, "E94.2.2.101", {"start": v(145.25, 114.5) * mm, "mid": v(144.66, 113.09) * mm, "end": v(143.25, 112.5) * mm});
            skArc(sketch, "E94.2.2.102", {"start": v(143.25, 127.5) * mm, "mid": v(144.66, 126.91) * mm, "end": v(145.25, 125.5) * mm});
            skArc(sketch, "E94.2.2.103", {"start": v(133.5, 112.5) * mm, "mid": v(132.09, 113.09) * mm, "end": v(131.5, 114.5) * mm});
            skArc(sketch, "E94.2.2.104", {"start": v(131.5, 125.5) * mm, "mid": v(132.09, 126.91) * mm, "end": v(133.5, 127.5) * mm});
            skArc(sketch, "E94.2.2.105", {"start": v(131.5, 94.5) * mm, "mid": v(132.09, 93.09) * mm, "end": v(133.5, 92.5) * mm});
            skArc(sketch, "E94.2.2.106", {"start": v(128.5, 94.5) * mm, "mid": v(127.91, 93.09) * mm, "end": v(126.5, 92.5) * mm});
            skArc(sketch, "E94.2.2.107", {"start": v(111.75, 105.5) * mm, "mid": v(111.16, 106.91) * mm, "end": v(109.75, 107.5) * mm});
            skArc(sketch, "E94.2.2.108", {"start": v(126.5, 107.5) * mm, "mid": v(127.91, 106.91) * mm, "end": v(128.5, 105.5) * mm});
            skLineSegment(sketch, "E94.2.2.109", {"start": v(155.12, 132.5) * mm, "end": v(157.13, 132.5) * mm});
            skArc(sketch, "E94.2.2.110", {"start": v(109.75, 127.5) * mm, "mid": v(111.16, 126.91) * mm, "end": v(111.75, 125.5) * mm});
            skArc(sketch, "E94.2.2.111", {"start": v(148.25, 114.5) * mm, "mid": v(148.84, 113.09) * mm, "end": v(150.25, 112.5) * mm});
            skLineSegment(sketch, "E94.2.2.112", {"start": v(155.12, 92.5) * mm, "end": v(157.13, 92.5) * mm});
            skArc(sketch, "E94.2.2.113", {"start": v(116.75, 92.5) * mm, "mid": v(115.34, 93.09) * mm, "end": v(114.75, 94.5) * mm});
            skLineSegment(sketch, "E94.2.2.114", {"start": v(155.12, 127.5) * mm, "end": v(157.13, 127.5) * mm});
            skArc(sketch, "E94.2.2.115", {"start": v(109.75, 92.5) * mm, "mid": v(111.16, 93.09) * mm, "end": v(111.75, 94.5) * mm});
            skArc(sketch, "E94.2.2.116", {"start": v(150.25, 92.5) * mm, "mid": v(148.84, 93.09) * mm, "end": v(148.25, 94.5) * mm});
            skLineSegment(sketch, "E94.direction1", {"start": v(-32, -17.5) * mm, "end": v(33, -17.5) * mm, "construction": true});
            skLineSegment(sketch, "E94.direction2", {"start": v(-32, -17.5) * mm, "end": v(-32, 37.5) * mm, "construction": true});
            skSolve(sketch);
        }
        {
            var Q0;
            Q0 = qSketchRegion(id + "F0", true);
            extrude(context, id + "F1", {"entities" : qUnion([Q0]), "depth" : .4 * mm});
        }
        {
            var Q0;
            Q0=qCreatedBy(makeId("Top.planeOp"),FACE);
            var sketch = newSketch(context, id + "F2", { "sketchPlane" : qUnion([Q0])});
            skLineSegment(sketch, "E95.bottom", {"start": v(165, 143) * mm, "end": v(-35, 143) * mm});
            skLineSegment(sketch, "E95.top", {"start": v(165, -32) * mm, "end": v(-35, -32) * mm});
            skLineSegment(sketch, "E95.left", {"start": v(165, 143) * mm, "end": v(165, -32) * mm});
            skLineSegment(sketch, "E95.right", {"start": v(-35, 143) * mm, "end": v(-35, -32) * mm});
            skSolve(sketch);
        }
        {
            var Q0;
            Q0=makeQuery(id+"F2.imprint","IMPRINT",FACE,{"disambiguationData":[TD([[makeQuery(id+"F2.imprint","IMPRINT",EDGE,{"derivedFrom":sQuery(id+"F2.wireOp",EDGE,"E95.bottom")}),1.0]])]});
            extrude(context, id + "F3", {"entities" : qUnion([Q0]), "oppositeDirection" : true, "depth" : 2 * mm});
        }
        {
            var Q0;
            Q0=makeQuery(id+"F3.opExtrude","SWEPT_BODY",BODY,{"disambiguationData":[OSD([sQuery(id+"F2.wireOp",EDGE,"E95.bottom"),sQuery(id+"F2.wireOp",EDGE,"E95.top"),sQuery(id+"F2.wireOp",EDGE,"E95.left"),sQuery(id+"F2.wireOp",EDGE,"E95.right")])]});
            transform(context, id + "F4", {"entities" : qUnion([Q0]), "transformType" : TransformType.TRANSLATION_3D, "dx" : 0 * mm, "dy" : 0 * mm, "dz" : .4 * mm, "makeCopy" : false});
        }
        {
            var Q0;
            Q0=makeQuery(id+"F1.opExtrude","SWEPT_BODY",BODY,{"disambiguationData":[OSD([sQuery(id+"F0.wireOp",EDGE,"E94.1.1.2"),sQuery(id+"F0.wireOp",EDGE,"E94.1.1.3"),sQuery(id+"F0.wireOp",EDGE,"E94.1.1.10"),sQuery(id+"F0.wireOp",EDGE,"E94.1.1.11"),sQuery(id+"F0.wireOp",EDGE,"E94.1.1.13"),sQuery(id+"F0.wireOp",EDGE,"E94.1.1.15"),sQuery(id+"F0.wireOp",EDGE,"E94.1.1.16"),sQuery(id+"F0.wireOp",EDGE,"E94.1.1.23"),sQuery(id+"F0.wireOp",EDGE,"E94.1.1.24"),sQuery(id+"F0.wireOp",EDGE,"E94.1.1.27"),sQuery(id+"F0.wireOp",EDGE,"E94.1.1.28"),sQuery(id+"F0.wireOp",EDGE,"E94.1.1.37"),sQuery(id+"F0.wireOp",EDGE,"E94.1.1.38"),sQuery(id+"F0.wireOp",EDGE,"E94.1.1.39"),sQuery(id+"F0.wireOp",EDGE,"E94.1.1.40"),sQuery(id+"F0.wireOp",EDGE,"E94.1.1.41"),sQuery(id+"F0.wireOp",EDGE,"E94.1.1.42"),sQuery(id+"F0.wireOp",EDGE,"E94.1.1.43"),sQuery(id+"F0.wireOp",EDGE,"E94.1.1.44"),sQuery(id+"F0.wireOp",EDGE,"E94.1.1.45"),sQuery(id+"F0.wireOp",EDGE,"E94.1.1.46"),sQuery(id+"F0.wireOp",EDGE,"E94.1.1.47"),sQuery(id+"F0.wireOp",EDGE,"E94.1.1.52"),sQuery(id+"F0.wireOp",EDGE,"E94.1.1.61"),sQuery(id+"F0.wireOp",EDGE,"E94.1.1.62"),sQuery(id+"F0.wireOp",EDGE,"E94.1.1.63"),sQuery(id+"F0.wireOp",EDGE,"E94.1.1.69"),sQuery(id+"F0.wireOp",EDGE,"E94.1.1.70"),sQuery(id+"F0.wireOp",EDGE,"E94.1.1.71"),sQuery(id+"F0.wireOp",EDGE,"E94.1.1.78"),sQuery(id+"F0.wireOp",EDGE,"E94.1.1.81"),sQuery(id+"F0.wireOp",EDGE,"E94.1.1.82"),sQuery(id+"F0.wireOp",EDGE,"E94.1.1.83"),sQuery(id+"F0.wireOp",EDGE,"E94.1.1.84"),sQuery(id+"F0.wireOp",EDGE,"E94.1.1.85"),sQuery(id+"F0.wireOp",EDGE,"E94.1.1.86"),sQuery(id+"F0.wireOp",EDGE,"E94.1.1.87"),sQuery(id+"F0.wireOp",EDGE,"E94.1.1.88"),sQuery(id+"F0.wireOp",EDGE,"E94.1.1.89"),sQuery(id+"F0.wireOp",EDGE,"E94.1.1.90"),sQuery(id+"F0.wireOp",EDGE,"E94.1.1.91"),sQuery(id+"F0.wireOp",EDGE,"E94.1.1.92"),sQuery(id+"F0.wireOp",EDGE,"E94.1.1.93"),sQuery(id+"F0.wireOp",EDGE,"E94.1.1.94"),sQuery(id+"F0.wireOp",EDGE,"E94.1.1.95"),sQuery(id+"F0.wireOp",EDGE,"E94.1.1.96"),sQuery(id+"F0.wireOp",EDGE,"E94.1.1.97"),sQuery(id+"F0.wireOp",EDGE,"E94.1.1.98"),sQuery(id+"F0.wireOp",EDGE,"E94.1.1.99"),sQuery(id+"F0.wireOp",EDGE,"E94.1.1.100"),sQuery(id+"F0.wireOp",EDGE,"E94.1.1.101"),sQuery(id+"F0.wireOp",EDGE,"E94.1.1.102"),sQuery(id+"F0.wireOp",EDGE,"E94.1.1.103"),sQuery(id+"F0.wireOp",EDGE,"E94.1.1.104"),sQuery(id+"F0.wireOp",EDGE,"E94.1.1.105"),sQuery(id+"F0.wireOp",EDGE,"E94.1.1.106"),sQuery(id+"F0.wireOp",EDGE,"E94.1.1.107"),sQuery(id+"F0.wireOp",EDGE,"E94.1.1.108"),sQuery(id+"F0.wireOp",EDGE,"E94.1.1.109"),sQuery(id+"F0.wireOp",EDGE,"E94.1.1.110"),sQuery(id+"F0.wireOp",EDGE,"E94.1.1.111"),sQuery(id+"F0.wireOp",EDGE,"E94.1.1.112"),sQuery(id+"F0.wireOp",EDGE,"E94.1.1.113"),sQuery(id+"F0.wireOp",EDGE,"E94.1.1.114"),sQuery(id+"F0.wireOp",EDGE,"E94.1.1.115"),sQuery(id+"F0.wireOp",EDGE,"E94.1.1.116")])]});
            var Q1;
            Q1=makeQuery(id+"F1.opExtrude","SWEPT_BODY",BODY,{"disambiguationData":[OSD([sQuery(id+"F0.wireOp",EDGE,"E0.bottom"),sQuery(id+"F0.wireOp",EDGE,"E0.top"),sQuery(id+"F0.wireOp",EDGE,"E0.left"),sQuery(id+"F0.wireOp",EDGE,"E0.right"),sQuery(id+"F0.wireOp",EDGE,"E1.filletArc"),sQuery(id+"F0.wireOp",EDGE,"E2.filletArc"),sQuery(id+"F0.wireOp",EDGE,"E3.filletArc"),sQuery(id+"F0.wireOp",EDGE,"E4.filletArc"),sQuery(id+"F0.wireOp",EDGE,"E5.MirrorCS"),sQuery(id+"F0.wireOp",EDGE,"E6.MirrorCS"),sQuery(id+"F0.wireOp",EDGE,"E7.MirrorCS"),sQuery(id+"F0.wireOp",EDGE,"E8.MirrorCS"),sQuery(id+"F0.wireOp",EDGE,"E9.MirrorCS"),sQuery(id+"F0.wireOp",EDGE,"E10.MirrorCS"),sQuery(id+"F0.wireOp",EDGE,"E15.MirrorCS"),sQuery(id+"F0.wireOp",EDGE,"E16.MirrorCS"),sQuery(id+"F0.wireOp",EDGE,"E17.MirrorCS"),sQuery(id+"F0.wireOp",EDGE,"E18.MirrorCS"),sQuery(id+"F0.wireOp",EDGE,"E19.MirrorCS"),sQuery(id+"F0.wireOp",EDGE,"E20.MirrorCS"),sQuery(id+"F0.wireOp",EDGE,"E21.MirrorCS"),sQuery(id+"F0.wireOp",EDGE,"E22.MirrorCS"),sQuery(id+"F0.wireOp",EDGE,"E23.MirrorCS"),sQuery(id+"F0.wireOp",EDGE,"E24.MirrorCS"),sQuery(id+"F0.wireOp",EDGE,"E26.MirrorCS"),sQuery(id+"F0.wireOp",EDGE,"E27.MirrorCS"),sQuery(id+"F0.wireOp",EDGE,"E29.MirrorCS"),sQuery(id+"F0.wireOp",EDGE,"E30.MirrorCS"),sQuery(id+"F0.wireOp",EDGE,"E31.MirrorCS"),sQuery(id+"F0.wireOp",EDGE,"E33.MirrorCS"),sQuery(id+"F0.wireOp",EDGE,"E34.MirrorCS"),sQuery(id+"F0.wireOp",EDGE,"E40.MirrorCS"),sQuery(id+"F0.wireOp",EDGE,"E42.MirrorCS"),sQuery(id+"F0.wireOp",EDGE,"E43.MirrorCS"),sQuery(id+"F0.wireOp",EDGE,"E44.MirrorCS"),sQuery(id+"F0.wireOp",EDGE,"E45.MirrorCS"),sQuery(id+"F0.wireOp",EDGE,"E46.MirrorCS"),sQuery(id+"F0.wireOp",EDGE,"E47.MirrorCS"),sQuery(id+"F0.wireOp",EDGE,"E50.MirrorCS"),sQuery(id+"F0.wireOp",EDGE,"E52.MirrorCS"),sQuery(id+"F0.wireOp",EDGE,"E53.MirrorCS"),sQuery(id+"F0.wireOp",EDGE,"E55.MirrorCS"),sQuery(id+"F0.wireOp",EDGE,"E56.bottom"),sQuery(id+"F0.wireOp",EDGE,"E56.top"),sQuery(id+"F0.wireOp",EDGE,"E57.MirrorCS"),sQuery(id+"F0.wireOp",EDGE,"E58.MirrorCS"),sQuery(id+"F0.wireOp",EDGE,"E59.MirrorCS"),sQuery(id+"F0.wireOp",EDGE,"E60.MirrorCS"),sQuery(id+"F0.wireOp",EDGE,"E62.MirrorCS"),sQuery(id+"F0.wireOp",EDGE,"E64.MirrorCS"),sQuery(id+"F0.wireOp",EDGE,"E56.right"),sQuery(id+"F0.wireOp",EDGE,"E69.MirrorCS"),sQuery(id+"F0.wireOp",EDGE,"E72.MirrorCS"),sQuery(id+"F0.wireOp",EDGE,"E73.MirrorCS"),sQuery(id+"F0.wireOp",EDGE,"E74.MirrorCS"),sQuery(id+"F0.wireOp",EDGE,"E83.trimOffspring"),sQuery(id+"F0.wireOp",EDGE,"E89.trimOffspring"),sQuery(id+"F0.wireOp",EDGE,"E91.bottom"),sQuery(id+"F0.wireOp",EDGE,"E91.top"),sQuery(id+"F0.wireOp",EDGE,"E91.right"),sQuery(id+"F0.wireOp",EDGE,"E92.bottom"),sQuery(id+"F0.wireOp",EDGE,"E92.top"),sQuery(id+"F0.wireOp",EDGE,"E92.right"),sQuery(id+"F0.wireOp",EDGE,"E93.bottom"),sQuery(id+"F0.wireOp",EDGE,"E93.top"),sQuery(id+"F0.wireOp",EDGE,"E93.right")])]});
            var Q2;
            Q2=makeQuery(id+"F1.opExtrude","SWEPT_BODY",BODY,{"disambiguationData":[OSD([sQuery(id+"F0.wireOp",EDGE,"E94.0.1.2"),sQuery(id+"F0.wireOp",EDGE,"E94.0.1.3"),sQuery(id+"F0.wireOp",EDGE,"E94.0.1.10"),sQuery(id+"F0.wireOp",EDGE,"E94.0.1.11"),sQuery(id+"F0.wireOp",EDGE,"E94.0.1.13"),sQuery(id+"F0.wireOp",EDGE,"E94.0.1.15"),sQuery(id+"F0.wireOp",EDGE,"E94.0.1.16"),sQuery(id+"F0.wireOp",EDGE,"E94.0.1.23"),sQuery(id+"F0.wireOp",EDGE,"E94.0.1.24"),sQuery(id+"F0.wireOp",EDGE,"E94.0.1.27"),sQuery(id+"F0.wireOp",EDGE,"E94.0.1.28"),sQuery(id+"F0.wireOp",EDGE,"E94.0.1.37"),sQuery(id+"F0.wireOp",EDGE,"E94.0.1.38"),sQuery(id+"F0.wireOp",EDGE,"E94.0.1.39"),sQuery(id+"F0.wireOp",EDGE,"E94.0.1.40"),sQuery(id+"F0.wireOp",EDGE,"E94.0.1.41"),sQuery(id+"F0.wireOp",EDGE,"E94.0.1.42"),sQuery(id+"F0.wireOp",EDGE,"E94.0.1.43"),sQuery(id+"F0.wireOp",EDGE,"E94.0.1.44"),sQuery(id+"F0.wireOp",EDGE,"E94.0.1.45"),sQuery(id+"F0.wireOp",EDGE,"E94.0.1.46"),sQuery(id+"F0.wireOp",EDGE,"E94.0.1.47"),sQuery(id+"F0.wireOp",EDGE,"E94.0.1.52"),sQuery(id+"F0.wireOp",EDGE,"E94.0.1.61"),sQuery(id+"F0.wireOp",EDGE,"E94.0.1.62"),sQuery(id+"F0.wireOp",EDGE,"E94.0.1.63"),sQuery(id+"F0.wireOp",EDGE,"E94.0.1.69"),sQuery(id+"F0.wireOp",EDGE,"E94.0.1.70"),sQuery(id+"F0.wireOp",EDGE,"E94.0.1.71"),sQuery(id+"F0.wireOp",EDGE,"E94.0.1.78"),sQuery(id+"F0.wireOp",EDGE,"E94.0.1.81"),sQuery(id+"F0.wireOp",EDGE,"E94.0.1.82"),sQuery(id+"F0.wireOp",EDGE,"E94.0.1.83"),sQuery(id+"F0.wireOp",EDGE,"E94.0.1.84"),sQuery(id+"F0.wireOp",EDGE,"E94.0.1.85"),sQuery(id+"F0.wireOp",EDGE,"E94.0.1.86"),sQuery(id+"F0.wireOp",EDGE,"E94.0.1.87"),sQuery(id+"F0.wireOp",EDGE,"E94.0.1.88"),sQuery(id+"F0.wireOp",EDGE,"E94.0.1.89"),sQuery(id+"F0.wireOp",EDGE,"E94.0.1.90"),sQuery(id+"F0.wireOp",EDGE,"E94.0.1.91"),sQuery(id+"F0.wireOp",EDGE,"E94.0.1.92"),sQuery(id+"F0.wireOp",EDGE,"E94.0.1.93"),sQuery(id+"F0.wireOp",EDGE,"E94.0.1.94"),sQuery(id+"F0.wireOp",EDGE,"E94.0.1.95"),sQuery(id+"F0.wireOp",EDGE,"E94.0.1.96"),sQuery(id+"F0.wireOp",EDGE,"E94.0.1.97"),sQuery(id+"F0.wireOp",EDGE,"E94.0.1.98"),sQuery(id+"F0.wireOp",EDGE,"E94.0.1.99"),sQuery(id+"F0.wireOp",EDGE,"E94.0.1.100"),sQuery(id+"F0.wireOp",EDGE,"E94.0.1.101"),sQuery(id+"F0.wireOp",EDGE,"E94.0.1.102"),sQuery(id+"F0.wireOp",EDGE,"E94.0.1.103"),sQuery(id+"F0.wireOp",EDGE,"E94.0.1.104"),sQuery(id+"F0.wireOp",EDGE,"E94.0.1.105"),sQuery(id+"F0.wireOp",EDGE,"E94.0.1.106"),sQuery(id+"F0.wireOp",EDGE,"E94.0.1.107"),sQuery(id+"F0.wireOp",EDGE,"E94.0.1.108"),sQuery(id+"F0.wireOp",EDGE,"E94.0.1.109"),sQuery(id+"F0.wireOp",EDGE,"E94.0.1.110"),sQuery(id+"F0.wireOp",EDGE,"E94.0.1.111"),sQuery(id+"F0.wireOp",EDGE,"E94.0.1.112"),sQuery(id+"F0.wireOp",EDGE,"E94.0.1.113"),sQuery(id+"F0.wireOp",EDGE,"E94.0.1.114"),sQuery(id+"F0.wireOp",EDGE,"E94.0.1.115"),sQuery(id+"F0.wireOp",EDGE,"E94.0.1.116")])]});
            var Q3;
            Q3=makeQuery(id+"F1.opExtrude","SWEPT_BODY",BODY,{"disambiguationData":[OSD([sQuery(id+"F0.wireOp",EDGE,"E94.0.2.2"),sQuery(id+"F0.wireOp",EDGE,"E94.0.2.3"),sQuery(id+"F0.wireOp",EDGE,"E94.0.2.10"),sQuery(id+"F0.wireOp",EDGE,"E94.0.2.11"),sQuery(id+"F0.wireOp",EDGE,"E94.0.2.13"),sQuery(id+"F0.wireOp",EDGE,"E94.0.2.15"),sQuery(id+"F0.wireOp",EDGE,"E94.0.2.16"),sQuery(id+"F0.wireOp",EDGE,"E94.0.2.23"),sQuery(id+"F0.wireOp",EDGE,"E94.0.2.24"),sQuery(id+"F0.wireOp",EDGE,"E94.0.2.27"),sQuery(id+"F0.wireOp",EDGE,"E94.0.2.28"),sQuery(id+"F0.wireOp",EDGE,"E94.0.2.37"),sQuery(id+"F0.wireOp",EDGE,"E94.0.2.38"),sQuery(id+"F0.wireOp",EDGE,"E94.0.2.39"),sQuery(id+"F0.wireOp",EDGE,"E94.0.2.40"),sQuery(id+"F0.wireOp",EDGE,"E94.0.2.41"),sQuery(id+"F0.wireOp",EDGE,"E94.0.2.42"),sQuery(id+"F0.wireOp",EDGE,"E94.0.2.43"),sQuery(id+"F0.wireOp",EDGE,"E94.0.2.44"),sQuery(id+"F0.wireOp",EDGE,"E94.0.2.45"),sQuery(id+"F0.wireOp",EDGE,"E94.0.2.46"),sQuery(id+"F0.wireOp",EDGE,"E94.0.2.47"),sQuery(id+"F0.wireOp",EDGE,"E94.0.2.52"),sQuery(id+"F0.wireOp",EDGE,"E94.0.2.61"),sQuery(id+"F0.wireOp",EDGE,"E94.0.2.62"),sQuery(id+"F0.wireOp",EDGE,"E94.0.2.63"),sQuery(id+"F0.wireOp",EDGE,"E94.0.2.69"),sQuery(id+"F0.wireOp",EDGE,"E94.0.2.70"),sQuery(id+"F0.wireOp",EDGE,"E94.0.2.71"),sQuery(id+"F0.wireOp",EDGE,"E94.0.2.78"),sQuery(id+"F0.wireOp",EDGE,"E94.0.2.81"),sQuery(id+"F0.wireOp",EDGE,"E94.0.2.82"),sQuery(id+"F0.wireOp",EDGE,"E94.0.2.83"),sQuery(id+"F0.wireOp",EDGE,"E94.0.2.84"),sQuery(id+"F0.wireOp",EDGE,"E94.0.2.85"),sQuery(id+"F0.wireOp",EDGE,"E94.0.2.86"),sQuery(id+"F0.wireOp",EDGE,"E94.0.2.87"),sQuery(id+"F0.wireOp",EDGE,"E94.0.2.88"),sQuery(id+"F0.wireOp",EDGE,"E94.0.2.89"),sQuery(id+"F0.wireOp",EDGE,"E94.0.2.90"),sQuery(id+"F0.wireOp",EDGE,"E94.0.2.91"),sQuery(id+"F0.wireOp",EDGE,"E94.0.2.92"),sQuery(id+"F0.wireOp",EDGE,"E94.0.2.93"),sQuery(id+"F0.wireOp",EDGE,"E94.0.2.94"),sQuery(id+"F0.wireOp",EDGE,"E94.0.2.95"),sQuery(id+"F0.wireOp",EDGE,"E94.0.2.96"),sQuery(id+"F0.wireOp",EDGE,"E94.0.2.97"),sQuery(id+"F0.wireOp",EDGE,"E94.0.2.98"),sQuery(id+"F0.wireOp",EDGE,"E94.0.2.99"),sQuery(id+"F0.wireOp",EDGE,"E94.0.2.100"),sQuery(id+"F0.wireOp",EDGE,"E94.0.2.101"),sQuery(id+"F0.wireOp",EDGE,"E94.0.2.102"),sQuery(id+"F0.wireOp",EDGE,"E94.0.2.103"),sQuery(id+"F0.wireOp",EDGE,"E94.0.2.104"),sQuery(id+"F0.wireOp",EDGE,"E94.0.2.105"),sQuery(id+"F0.wireOp",EDGE,"E94.0.2.106"),sQuery(id+"F0.wireOp",EDGE,"E94.0.2.107"),sQuery(id+"F0.wireOp",EDGE,"E94.0.2.108"),sQuery(id+"F0.wireOp",EDGE,"E94.0.2.109"),sQuery(id+"F0.wireOp",EDGE,"E94.0.2.110"),sQuery(id+"F0.wireOp",EDGE,"E94.0.2.111"),sQuery(id+"F0.wireOp",EDGE,"E94.0.2.112"),sQuery(id+"F0.wireOp",EDGE,"E94.0.2.113"),sQuery(id+"F0.wireOp",EDGE,"E94.0.2.114"),sQuery(id+"F0.wireOp",EDGE,"E94.0.2.115"),sQuery(id+"F0.wireOp",EDGE,"E94.0.2.116")])]});
            var Q4;
            Q4=makeQuery(id+"F1.opExtrude","SWEPT_BODY",BODY,{"disambiguationData":[OSD([sQuery(id+"F0.wireOp",EDGE,"E94.1.2.2"),sQuery(id+"F0.wireOp",EDGE,"E94.1.2.3"),sQuery(id+"F0.wireOp",EDGE,"E94.1.2.10"),sQuery(id+"F0.wireOp",EDGE,"E94.1.2.11"),sQuery(id+"F0.wireOp",EDGE,"E94.1.2.13"),sQuery(id+"F0.wireOp",EDGE,"E94.1.2.15"),sQuery(id+"F0.wireOp",EDGE,"E94.1.2.16"),sQuery(id+"F0.wireOp",EDGE,"E94.1.2.23"),sQuery(id+"F0.wireOp",EDGE,"E94.1.2.24"),sQuery(id+"F0.wireOp",EDGE,"E94.1.2.27"),sQuery(id+"F0.wireOp",EDGE,"E94.1.2.28"),sQuery(id+"F0.wireOp",EDGE,"E94.1.2.37"),sQuery(id+"F0.wireOp",EDGE,"E94.1.2.38"),sQuery(id+"F0.wireOp",EDGE,"E94.1.2.39"),sQuery(id+"F0.wireOp",EDGE,"E94.1.2.40"),sQuery(id+"F0.wireOp",EDGE,"E94.1.2.41"),sQuery(id+"F0.wireOp",EDGE,"E94.1.2.42"),sQuery(id+"F0.wireOp",EDGE,"E94.1.2.43"),sQuery(id+"F0.wireOp",EDGE,"E94.1.2.44"),sQuery(id+"F0.wireOp",EDGE,"E94.1.2.45"),sQuery(id+"F0.wireOp",EDGE,"E94.1.2.46"),sQuery(id+"F0.wireOp",EDGE,"E94.1.2.47"),sQuery(id+"F0.wireOp",EDGE,"E94.1.2.52"),sQuery(id+"F0.wireOp",EDGE,"E94.1.2.61"),sQuery(id+"F0.wireOp",EDGE,"E94.1.2.62"),sQuery(id+"F0.wireOp",EDGE,"E94.1.2.63"),sQuery(id+"F0.wireOp",EDGE,"E94.1.2.69"),sQuery(id+"F0.wireOp",EDGE,"E94.1.2.70"),sQuery(id+"F0.wireOp",EDGE,"E94.1.2.71"),sQuery(id+"F0.wireOp",EDGE,"E94.1.2.78"),sQuery(id+"F0.wireOp",EDGE,"E94.1.2.81"),sQuery(id+"F0.wireOp",EDGE,"E94.1.2.82"),sQuery(id+"F0.wireOp",EDGE,"E94.1.2.83"),sQuery(id+"F0.wireOp",EDGE,"E94.1.2.84"),sQuery(id+"F0.wireOp",EDGE,"E94.1.2.85"),sQuery(id+"F0.wireOp",EDGE,"E94.1.2.86"),sQuery(id+"F0.wireOp",EDGE,"E94.1.2.87"),sQuery(id+"F0.wireOp",EDGE,"E94.1.2.88"),sQuery(id+"F0.wireOp",EDGE,"E94.1.2.89"),sQuery(id+"F0.wireOp",EDGE,"E94.1.2.90"),sQuery(id+"F0.wireOp",EDGE,"E94.1.2.91"),sQuery(id+"F0.wireOp",EDGE,"E94.1.2.92"),sQuery(id+"F0.wireOp",EDGE,"E94.1.2.93"),sQuery(id+"F0.wireOp",EDGE,"E94.1.2.94"),sQuery(id+"F0.wireOp",EDGE,"E94.1.2.95"),sQuery(id+"F0.wireOp",EDGE,"E94.1.2.96"),sQuery(id+"F0.wireOp",EDGE,"E94.1.2.97"),sQuery(id+"F0.wireOp",EDGE,"E94.1.2.98"),sQuery(id+"F0.wireOp",EDGE,"E94.1.2.99"),sQuery(id+"F0.wireOp",EDGE,"E94.1.2.100"),sQuery(id+"F0.wireOp",EDGE,"E94.1.2.101"),sQuery(id+"F0.wireOp",EDGE,"E94.1.2.102"),sQuery(id+"F0.wireOp",EDGE,"E94.1.2.103"),sQuery(id+"F0.wireOp",EDGE,"E94.1.2.104"),sQuery(id+"F0.wireOp",EDGE,"E94.1.2.105"),sQuery(id+"F0.wireOp",EDGE,"E94.1.2.106"),sQuery(id+"F0.wireOp",EDGE,"E94.1.2.107"),sQuery(id+"F0.wireOp",EDGE,"E94.1.2.108"),sQuery(id+"F0.wireOp",EDGE,"E94.1.2.109"),sQuery(id+"F0.wireOp",EDGE,"E94.1.2.110"),sQuery(id+"F0.wireOp",EDGE,"E94.1.2.111"),sQuery(id+"F0.wireOp",EDGE,"E94.1.2.112"),sQuery(id+"F0.wireOp",EDGE,"E94.1.2.113"),sQuery(id+"F0.wireOp",EDGE,"E94.1.2.114"),sQuery(id+"F0.wireOp",EDGE,"E94.1.2.115"),sQuery(id+"F0.wireOp",EDGE,"E94.1.2.116")])]});
            var Q5;
            Q5=makeQuery(id+"F1.opExtrude","SWEPT_BODY",BODY,{"disambiguationData":[OSD([sQuery(id+"F0.wireOp",EDGE,"E94.2.0.2"),sQuery(id+"F0.wireOp",EDGE,"E94.2.0.3"),sQuery(id+"F0.wireOp",EDGE,"E94.2.0.10"),sQuery(id+"F0.wireOp",EDGE,"E94.2.0.11"),sQuery(id+"F0.wireOp",EDGE,"E94.2.0.13"),sQuery(id+"F0.wireOp",EDGE,"E94.2.0.15"),sQuery(id+"F0.wireOp",EDGE,"E94.2.0.16"),sQuery(id+"F0.wireOp",EDGE,"E94.2.0.23"),sQuery(id+"F0.wireOp",EDGE,"E94.2.0.24"),sQuery(id+"F0.wireOp",EDGE,"E94.2.0.27"),sQuery(id+"F0.wireOp",EDGE,"E94.2.0.28"),sQuery(id+"F0.wireOp",EDGE,"E94.2.0.37"),sQuery(id+"F0.wireOp",EDGE,"E94.2.0.38"),sQuery(id+"F0.wireOp",EDGE,"E94.2.0.39"),sQuery(id+"F0.wireOp",EDGE,"E94.2.0.40"),sQuery(id+"F0.wireOp",EDGE,"E94.2.0.41"),sQuery(id+"F0.wireOp",EDGE,"E94.2.0.42"),sQuery(id+"F0.wireOp",EDGE,"E94.2.0.43"),sQuery(id+"F0.wireOp",EDGE,"E94.2.0.44"),sQuery(id+"F0.wireOp",EDGE,"E94.2.0.45"),sQuery(id+"F0.wireOp",EDGE,"E94.2.0.46"),sQuery(id+"F0.wireOp",EDGE,"E94.2.0.47"),sQuery(id+"F0.wireOp",EDGE,"E94.2.0.52"),sQuery(id+"F0.wireOp",EDGE,"E94.2.0.61"),sQuery(id+"F0.wireOp",EDGE,"E94.2.0.62"),sQuery(id+"F0.wireOp",EDGE,"E94.2.0.63"),sQuery(id+"F0.wireOp",EDGE,"E94.2.0.69"),sQuery(id+"F0.wireOp",EDGE,"E94.2.0.70"),sQuery(id+"F0.wireOp",EDGE,"E94.2.0.71"),sQuery(id+"F0.wireOp",EDGE,"E94.2.0.78"),sQuery(id+"F0.wireOp",EDGE,"E94.2.0.81"),sQuery(id+"F0.wireOp",EDGE,"E94.2.0.82"),sQuery(id+"F0.wireOp",EDGE,"E94.2.0.83"),sQuery(id+"F0.wireOp",EDGE,"E94.2.0.84"),sQuery(id+"F0.wireOp",EDGE,"E94.2.0.85"),sQuery(id+"F0.wireOp",EDGE,"E94.2.0.86"),sQuery(id+"F0.wireOp",EDGE,"E94.2.0.87"),sQuery(id+"F0.wireOp",EDGE,"E94.2.0.88"),sQuery(id+"F0.wireOp",EDGE,"E94.2.0.89"),sQuery(id+"F0.wireOp",EDGE,"E94.2.0.90"),sQuery(id+"F0.wireOp",EDGE,"E94.2.0.91"),sQuery(id+"F0.wireOp",EDGE,"E94.2.0.92"),sQuery(id+"F0.wireOp",EDGE,"E94.2.0.93"),sQuery(id+"F0.wireOp",EDGE,"E94.2.0.94"),sQuery(id+"F0.wireOp",EDGE,"E94.2.0.95"),sQuery(id+"F0.wireOp",EDGE,"E94.2.0.96"),sQuery(id+"F0.wireOp",EDGE,"E94.2.0.97"),sQuery(id+"F0.wireOp",EDGE,"E94.2.0.98"),sQuery(id+"F0.wireOp",EDGE,"E94.2.0.99"),sQuery(id+"F0.wireOp",EDGE,"E94.2.0.100"),sQuery(id+"F0.wireOp",EDGE,"E94.2.0.101"),sQuery(id+"F0.wireOp",EDGE,"E94.2.0.102"),sQuery(id+"F0.wireOp",EDGE,"E94.2.0.103"),sQuery(id+"F0.wireOp",EDGE,"E94.2.0.104"),sQuery(id+"F0.wireOp",EDGE,"E94.2.0.105"),sQuery(id+"F0.wireOp",EDGE,"E94.2.0.106"),sQuery(id+"F0.wireOp",EDGE,"E94.2.0.107"),sQuery(id+"F0.wireOp",EDGE,"E94.2.0.108"),sQuery(id+"F0.wireOp",EDGE,"E94.2.0.109"),sQuery(id+"F0.wireOp",EDGE,"E94.2.0.110"),sQuery(id+"F0.wireOp",EDGE,"E94.2.0.111"),sQuery(id+"F0.wireOp",EDGE,"E94.2.0.112"),sQuery(id+"F0.wireOp",EDGE,"E94.2.0.113"),sQuery(id+"F0.wireOp",EDGE,"E94.2.0.114"),sQuery(id+"F0.wireOp",EDGE,"E94.2.0.115"),sQuery(id+"F0.wireOp",EDGE,"E94.2.0.116")])]});
            var Q6;
            Q6=makeQuery(id+"F1.opExtrude","SWEPT_BODY",BODY,{"disambiguationData":[OSD([sQuery(id+"F0.wireOp",EDGE,"E94.2.2.2"),sQuery(id+"F0.wireOp",EDGE,"E94.2.2.3"),sQuery(id+"F0.wireOp",EDGE,"E94.2.2.10"),sQuery(id+"F0.wireOp",EDGE,"E94.2.2.11"),sQuery(id+"F0.wireOp",EDGE,"E94.2.2.13"),sQuery(id+"F0.wireOp",EDGE,"E94.2.2.15"),sQuery(id+"F0.wireOp",EDGE,"E94.2.2.16"),sQuery(id+"F0.wireOp",EDGE,"E94.2.2.23"),sQuery(id+"F0.wireOp",EDGE,"E94.2.2.24"),sQuery(id+"F0.wireOp",EDGE,"E94.2.2.27"),sQuery(id+"F0.wireOp",EDGE,"E94.2.2.28"),sQuery(id+"F0.wireOp",EDGE,"E94.2.2.37"),sQuery(id+"F0.wireOp",EDGE,"E94.2.2.38"),sQuery(id+"F0.wireOp",EDGE,"E94.2.2.39"),sQuery(id+"F0.wireOp",EDGE,"E94.2.2.40"),sQuery(id+"F0.wireOp",EDGE,"E94.2.2.41"),sQuery(id+"F0.wireOp",EDGE,"E94.2.2.42"),sQuery(id+"F0.wireOp",EDGE,"E94.2.2.43"),sQuery(id+"F0.wireOp",EDGE,"E94.2.2.44"),sQuery(id+"F0.wireOp",EDGE,"E94.2.2.45"),sQuery(id+"F0.wireOp",EDGE,"E94.2.2.46"),sQuery(id+"F0.wireOp",EDGE,"E94.2.2.47"),sQuery(id+"F0.wireOp",EDGE,"E94.2.2.52"),sQuery(id+"F0.wireOp",EDGE,"E94.2.2.61"),sQuery(id+"F0.wireOp",EDGE,"E94.2.2.62"),sQuery(id+"F0.wireOp",EDGE,"E94.2.2.63"),sQuery(id+"F0.wireOp",EDGE,"E94.2.2.69"),sQuery(id+"F0.wireOp",EDGE,"E94.2.2.70"),sQuery(id+"F0.wireOp",EDGE,"E94.2.2.71"),sQuery(id+"F0.wireOp",EDGE,"E94.2.2.78"),sQuery(id+"F0.wireOp",EDGE,"E94.2.2.81"),sQuery(id+"F0.wireOp",EDGE,"E94.2.2.82"),sQuery(id+"F0.wireOp",EDGE,"E94.2.2.83"),sQuery(id+"F0.wireOp",EDGE,"E94.2.2.84"),sQuery(id+"F0.wireOp",EDGE,"E94.2.2.85"),sQuery(id+"F0.wireOp",EDGE,"E94.2.2.86"),sQuery(id+"F0.wireOp",EDGE,"E94.2.2.87"),sQuery(id+"F0.wireOp",EDGE,"E94.2.2.88"),sQuery(id+"F0.wireOp",EDGE,"E94.2.2.89"),sQuery(id+"F0.wireOp",EDGE,"E94.2.2.90"),sQuery(id+"F0.wireOp",EDGE,"E94.2.2.91"),sQuery(id+"F0.wireOp",EDGE,"E94.2.2.92"),sQuery(id+"F0.wireOp",EDGE,"E94.2.2.93"),sQuery(id+"F0.wireOp",EDGE,"E94.2.2.94"),sQuery(id+"F0.wireOp",EDGE,"E94.2.2.95"),sQuery(id+"F0.wireOp",EDGE,"E94.2.2.96"),sQuery(id+"F0.wireOp",EDGE,"E94.2.2.97"),sQuery(id+"F0.wireOp",EDGE,"E94.2.2.98"),sQuery(id+"F0.wireOp",EDGE,"E94.2.2.99"),sQuery(id+"F0.wireOp",EDGE,"E94.2.2.100"),sQuery(id+"F0.wireOp",EDGE,"E94.2.2.101"),sQuery(id+"F0.wireOp",EDGE,"E94.2.2.102"),sQuery(id+"F0.wireOp",EDGE,"E94.2.2.103"),sQuery(id+"F0.wireOp",EDGE,"E94.2.2.104"),sQuery(id+"F0.wireOp",EDGE,"E94.2.2.105"),sQuery(id+"F0.wireOp",EDGE,"E94.2.2.106"),sQuery(id+"F0.wireOp",EDGE,"E94.2.2.107"),sQuery(id+"F0.wireOp",EDGE,"E94.2.2.108"),sQuery(id+"F0.wireOp",EDGE,"E94.2.2.109"),sQuery(id+"F0.wireOp",EDGE,"E94.2.2.110"),sQuery(id+"F0.wireOp",EDGE,"E94.2.2.111"),sQuery(id+"F0.wireOp",EDGE,"E94.2.2.112"),sQuery(id+"F0.wireOp",EDGE,"E94.2.2.113"),sQuery(id+"F0.wireOp",EDGE,"E94.2.2.114"),sQuery(id+"F0.wireOp",EDGE,"E94.2.2.115"),sQuery(id+"F0.wireOp",EDGE,"E94.2.2.116")])]});
            var Q7;
            Q7=makeQuery(id+"F1.opExtrude","SWEPT_BODY",BODY,{"disambiguationData":[OSD([sQuery(id+"F0.wireOp",EDGE,"E94.2.1.2"),sQuery(id+"F0.wireOp",EDGE,"E94.2.1.3"),sQuery(id+"F0.wireOp",EDGE,"E94.2.1.10"),sQuery(id+"F0.wireOp",EDGE,"E94.2.1.11"),sQuery(id+"F0.wireOp",EDGE,"E94.2.1.13"),sQuery(id+"F0.wireOp",EDGE,"E94.2.1.15"),sQuery(id+"F0.wireOp",EDGE,"E94.2.1.16"),sQuery(id+"F0.wireOp",EDGE,"E94.2.1.23"),sQuery(id+"F0.wireOp",EDGE,"E94.2.1.24"),sQuery(id+"F0.wireOp",EDGE,"E94.2.1.27"),sQuery(id+"F0.wireOp",EDGE,"E94.2.1.28"),sQuery(id+"F0.wireOp",EDGE,"E94.2.1.37"),sQuery(id+"F0.wireOp",EDGE,"E94.2.1.38"),sQuery(id+"F0.wireOp",EDGE,"E94.2.1.39"),sQuery(id+"F0.wireOp",EDGE,"E94.2.1.40"),sQuery(id+"F0.wireOp",EDGE,"E94.2.1.41"),sQuery(id+"F0.wireOp",EDGE,"E94.2.1.42"),sQuery(id+"F0.wireOp",EDGE,"E94.2.1.43"),sQuery(id+"F0.wireOp",EDGE,"E94.2.1.44"),sQuery(id+"F0.wireOp",EDGE,"E94.2.1.45"),sQuery(id+"F0.wireOp",EDGE,"E94.2.1.46"),sQuery(id+"F0.wireOp",EDGE,"E94.2.1.47"),sQuery(id+"F0.wireOp",EDGE,"E94.2.1.52"),sQuery(id+"F0.wireOp",EDGE,"E94.2.1.61"),sQuery(id+"F0.wireOp",EDGE,"E94.2.1.62"),sQuery(id+"F0.wireOp",EDGE,"E94.2.1.63"),sQuery(id+"F0.wireOp",EDGE,"E94.2.1.69"),sQuery(id+"F0.wireOp",EDGE,"E94.2.1.70"),sQuery(id+"F0.wireOp",EDGE,"E94.2.1.71"),sQuery(id+"F0.wireOp",EDGE,"E94.2.1.78"),sQuery(id+"F0.wireOp",EDGE,"E94.2.1.81"),sQuery(id+"F0.wireOp",EDGE,"E94.2.1.82"),sQuery(id+"F0.wireOp",EDGE,"E94.2.1.83"),sQuery(id+"F0.wireOp",EDGE,"E94.2.1.84"),sQuery(id+"F0.wireOp",EDGE,"E94.2.1.85"),sQuery(id+"F0.wireOp",EDGE,"E94.2.1.86"),sQuery(id+"F0.wireOp",EDGE,"E94.2.1.87"),sQuery(id+"F0.wireOp",EDGE,"E94.2.1.88"),sQuery(id+"F0.wireOp",EDGE,"E94.2.1.89"),sQuery(id+"F0.wireOp",EDGE,"E94.2.1.90"),sQuery(id+"F0.wireOp",EDGE,"E94.2.1.91"),sQuery(id+"F0.wireOp",EDGE,"E94.2.1.92"),sQuery(id+"F0.wireOp",EDGE,"E94.2.1.93"),sQuery(id+"F0.wireOp",EDGE,"E94.2.1.94"),sQuery(id+"F0.wireOp",EDGE,"E94.2.1.95"),sQuery(id+"F0.wireOp",EDGE,"E94.2.1.96"),sQuery(id+"F0.wireOp",EDGE,"E94.2.1.97"),sQuery(id+"F0.wireOp",EDGE,"E94.2.1.98"),sQuery(id+"F0.wireOp",EDGE,"E94.2.1.99"),sQuery(id+"F0.wireOp",EDGE,"E94.2.1.100"),sQuery(id+"F0.wireOp",EDGE,"E94.2.1.101"),sQuery(id+"F0.wireOp",EDGE,"E94.2.1.102"),sQuery(id+"F0.wireOp",EDGE,"E94.2.1.103"),sQuery(id+"F0.wireOp",EDGE,"E94.2.1.104"),sQuery(id+"F0.wireOp",EDGE,"E94.2.1.105"),sQuery(id+"F0.wireOp",EDGE,"E94.2.1.106"),sQuery(id+"F0.wireOp",EDGE,"E94.2.1.107"),sQuery(id+"F0.wireOp",EDGE,"E94.2.1.108"),sQuery(id+"F0.wireOp",EDGE,"E94.2.1.109"),sQuery(id+"F0.wireOp",EDGE,"E94.2.1.110"),sQuery(id+"F0.wireOp",EDGE,"E94.2.1.111"),sQuery(id+"F0.wireOp",EDGE,"E94.2.1.112"),sQuery(id+"F0.wireOp",EDGE,"E94.2.1.113"),sQuery(id+"F0.wireOp",EDGE,"E94.2.1.114"),sQuery(id+"F0.wireOp",EDGE,"E94.2.1.115"),sQuery(id+"F0.wireOp",EDGE,"E94.2.1.116")])]});
            var Q8;
            Q8=makeQuery(id+"F1.opExtrude","SWEPT_BODY",BODY,{"disambiguationData":[OSD([sQuery(id+"F0.wireOp",EDGE,"E94.1.0.2"),sQuery(id+"F0.wireOp",EDGE,"E94.1.0.3"),sQuery(id+"F0.wireOp",EDGE,"E94.1.0.10"),sQuery(id+"F0.wireOp",EDGE,"E94.1.0.11"),sQuery(id+"F0.wireOp",EDGE,"E94.1.0.13"),sQuery(id+"F0.wireOp",EDGE,"E94.1.0.15"),sQuery(id+"F0.wireOp",EDGE,"E94.1.0.16"),sQuery(id+"F0.wireOp",EDGE,"E94.1.0.23"),sQuery(id+"F0.wireOp",EDGE,"E94.1.0.24"),sQuery(id+"F0.wireOp",EDGE,"E94.1.0.27"),sQuery(id+"F0.wireOp",EDGE,"E94.1.0.28"),sQuery(id+"F0.wireOp",EDGE,"E94.1.0.37"),sQuery(id+"F0.wireOp",EDGE,"E94.1.0.38"),sQuery(id+"F0.wireOp",EDGE,"E94.1.0.39"),sQuery(id+"F0.wireOp",EDGE,"E94.1.0.40"),sQuery(id+"F0.wireOp",EDGE,"E94.1.0.41"),sQuery(id+"F0.wireOp",EDGE,"E94.1.0.42"),sQuery(id+"F0.wireOp",EDGE,"E94.1.0.43"),sQuery(id+"F0.wireOp",EDGE,"E94.1.0.44"),sQuery(id+"F0.wireOp",EDGE,"E94.1.0.45"),sQuery(id+"F0.wireOp",EDGE,"E94.1.0.46"),sQuery(id+"F0.wireOp",EDGE,"E94.1.0.47"),sQuery(id+"F0.wireOp",EDGE,"E94.1.0.52"),sQuery(id+"F0.wireOp",EDGE,"E94.1.0.61"),sQuery(id+"F0.wireOp",EDGE,"E94.1.0.62"),sQuery(id+"F0.wireOp",EDGE,"E94.1.0.63"),sQuery(id+"F0.wireOp",EDGE,"E94.1.0.69"),sQuery(id+"F0.wireOp",EDGE,"E94.1.0.70"),sQuery(id+"F0.wireOp",EDGE,"E94.1.0.71"),sQuery(id+"F0.wireOp",EDGE,"E94.1.0.78"),sQuery(id+"F0.wireOp",EDGE,"E94.1.0.81"),sQuery(id+"F0.wireOp",EDGE,"E94.1.0.82"),sQuery(id+"F0.wireOp",EDGE,"E94.1.0.83"),sQuery(id+"F0.wireOp",EDGE,"E94.1.0.84"),sQuery(id+"F0.wireOp",EDGE,"E94.1.0.85"),sQuery(id+"F0.wireOp",EDGE,"E94.1.0.86"),sQuery(id+"F0.wireOp",EDGE,"E94.1.0.87"),sQuery(id+"F0.wireOp",EDGE,"E94.1.0.88"),sQuery(id+"F0.wireOp",EDGE,"E94.1.0.89"),sQuery(id+"F0.wireOp",EDGE,"E94.1.0.90"),sQuery(id+"F0.wireOp",EDGE,"E94.1.0.91"),sQuery(id+"F0.wireOp",EDGE,"E94.1.0.92"),sQuery(id+"F0.wireOp",EDGE,"E94.1.0.93"),sQuery(id+"F0.wireOp",EDGE,"E94.1.0.94"),sQuery(id+"F0.wireOp",EDGE,"E94.1.0.95"),sQuery(id+"F0.wireOp",EDGE,"E94.1.0.96"),sQuery(id+"F0.wireOp",EDGE,"E94.1.0.97"),sQuery(id+"F0.wireOp",EDGE,"E94.1.0.98"),sQuery(id+"F0.wireOp",EDGE,"E94.1.0.99"),sQuery(id+"F0.wireOp",EDGE,"E94.1.0.100"),sQuery(id+"F0.wireOp",EDGE,"E94.1.0.101"),sQuery(id+"F0.wireOp",EDGE,"E94.1.0.102"),sQuery(id+"F0.wireOp",EDGE,"E94.1.0.103"),sQuery(id+"F0.wireOp",EDGE,"E94.1.0.104"),sQuery(id+"F0.wireOp",EDGE,"E94.1.0.105"),sQuery(id+"F0.wireOp",EDGE,"E94.1.0.106"),sQuery(id+"F0.wireOp",EDGE,"E94.1.0.107"),sQuery(id+"F0.wireOp",EDGE,"E94.1.0.108"),sQuery(id+"F0.wireOp",EDGE,"E94.1.0.109"),sQuery(id+"F0.wireOp",EDGE,"E94.1.0.110"),sQuery(id+"F0.wireOp",EDGE,"E94.1.0.111"),sQuery(id+"F0.wireOp",EDGE,"E94.1.0.112"),sQuery(id+"F0.wireOp",EDGE,"E94.1.0.113"),sQuery(id+"F0.wireOp",EDGE,"E94.1.0.114"),sQuery(id+"F0.wireOp",EDGE,"E94.1.0.115"),sQuery(id+"F0.wireOp",EDGE,"E94.1.0.116")])]});
            var Q9;
            Q9=makeQuery(id+"F3.opExtrude","SWEPT_BODY",BODY,{"disambiguationData":[OSD([sQuery(id+"F2.wireOp",EDGE,"E95.bottom"),sQuery(id+"F2.wireOp",EDGE,"E95.top"),sQuery(id+"F2.wireOp",EDGE,"E95.left"),sQuery(id+"F2.wireOp",EDGE,"E95.right")])]});
            booleanBodies(context, id + "F5", {"operationType" : BooleanOperationType.SUBTRACTION, "tools" : qUnion([Q0, Q1, Q2, Q3, Q4, Q5, Q6, Q7, Q8]), "targets" : qUnion([Q9])});
        }
    });
